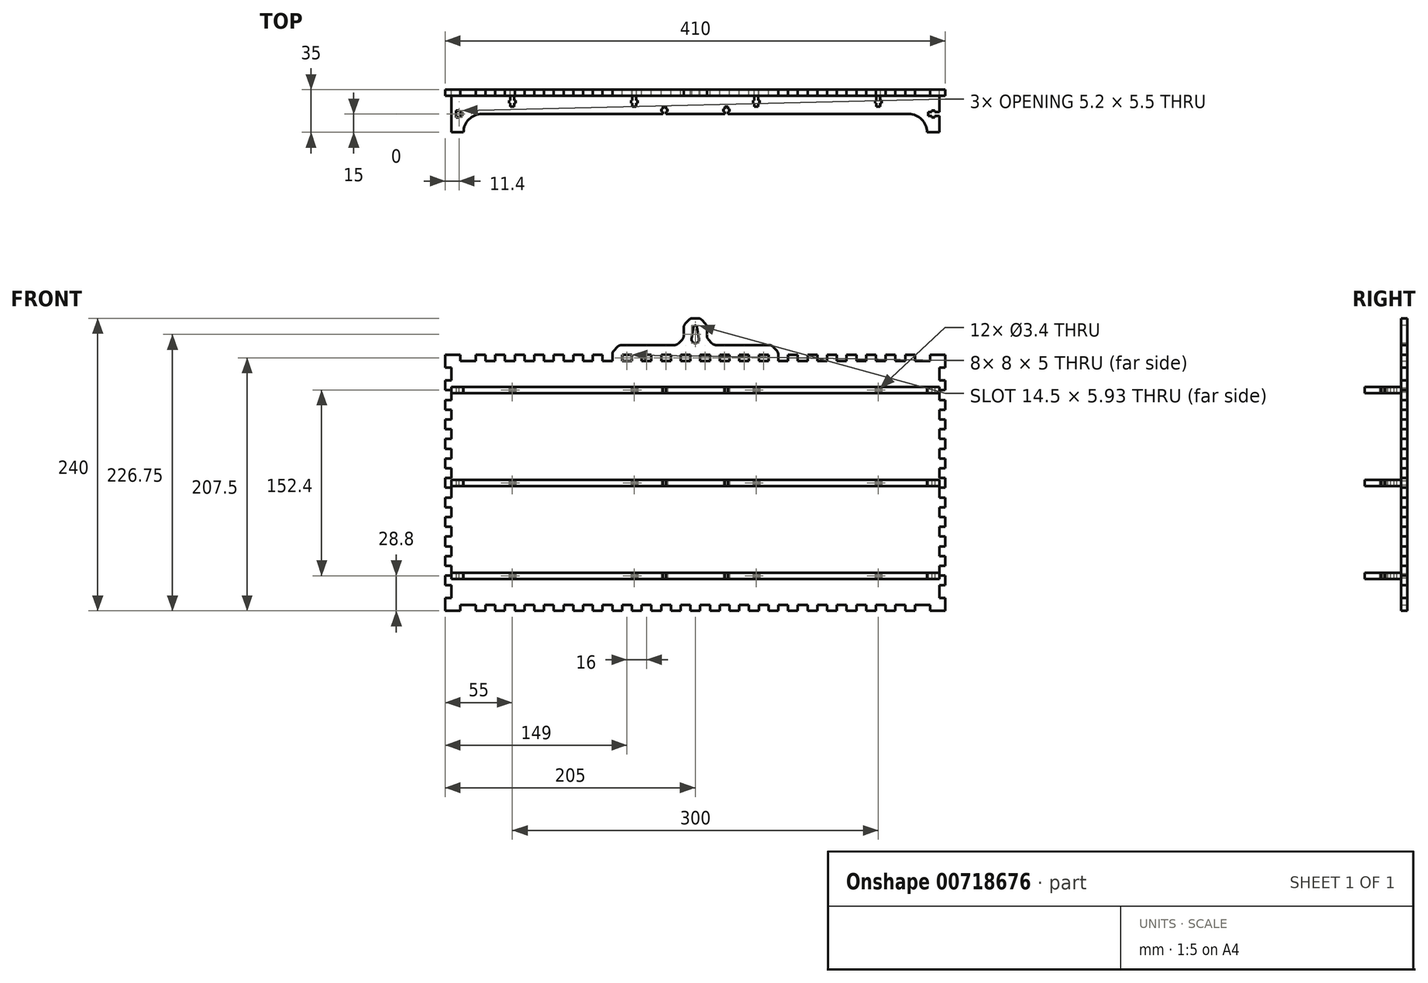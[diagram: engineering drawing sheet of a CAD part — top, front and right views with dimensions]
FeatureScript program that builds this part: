
annotation { "Feature Type Name" : "Feature", "Feature Type Description" : "" }
export const myFeature = defineFeature(function(context is Context, id is Id, definition is map)
    precondition{}
    {
        {
            var Q0;
            Q0=qCreatedBy(makeId("Front.planeOp"),FACE);
            var sketch = newSketch(context, id + "F0", { "sketchPlane" : qUnion([Q0])});
            skLineSegment(sketch, "E0", {"start": v(-100, 105) * mm, "end": v(-92, 105) * mm});
            skLineSegment(sketch, "E1", {"start": v(-92, 105) * mm, "end": v(-92, 100) * mm});
            skLineSegment(sketch, "E2", {"start": v(-92, 100) * mm, "end": v(-84, 100) * mm});
            skLineSegment(sketch, "E3", {"start": v(-84, 100) * mm, "end": v(-84, 105) * mm});
            skLineSegment(sketch, "E4", {"start": v(-84, 105) * mm, "end": v(-76, 105) * mm});
            skLineSegment(sketch, "E5", {"start": v(-76, 105) * mm, "end": v(-76, 100) * mm});
            skLineSegment(sketch, "E6", {"start": v(-76, 100) * mm, "end": v(-68, 100) * mm});
            skLineSegment(sketch, "E7", {"start": v(-68, 100) * mm, "end": v(-68, 105) * mm});
            skLineSegment(sketch, "E8", {"start": v(-68, 105) * mm, "end": v(-60, 105) * mm});
            skLineSegment(sketch, "E9", {"start": v(-60, 105) * mm, "end": v(-60, 100) * mm});
            skLineSegment(sketch, "E10", {"start": v(-60, 100) * mm, "end": v(-52, 100) * mm});
            skLineSegment(sketch, "E11", {"start": v(-52, 100) * mm, "end": v(-52, 105) * mm});
            skLineSegment(sketch, "E12", {"start": v(-52, 105) * mm, "end": v(-44, 105) * mm});
            skLineSegment(sketch, "E13", {"start": v(-44, 105) * mm, "end": v(-44, 100) * mm});
            skLineSegment(sketch, "E14", {"start": v(-44, 100) * mm, "end": v(-36, 100) * mm});
            skLineSegment(sketch, "E15", {"start": v(-36, 100) * mm, "end": v(-36, 105) * mm});
            skLineSegment(sketch, "E16", {"start": v(-36, 105) * mm, "end": v(-28, 105) * mm});
            skLineSegment(sketch, "E17", {"start": v(-28, 105) * mm, "end": v(-28, 100) * mm});
            skLineSegment(sketch, "E18", {"start": v(-28, 100) * mm, "end": v(-20, 100) * mm});
            skLineSegment(sketch, "E19", {"start": v(-20, 100) * mm, "end": v(-20, 105) * mm});
            skLineSegment(sketch, "E20", {"start": v(-20, 105) * mm, "end": v(-12, 105) * mm});
            skLineSegment(sketch, "E21", {"start": v(-12, 105) * mm, "end": v(-12, 100) * mm});
            skLineSegment(sketch, "E22", {"start": v(-12, 100) * mm, "end": v(-4, 100) * mm});
            skLineSegment(sketch, "E23", {"start": v(-4, 100) * mm, "end": v(-4, 105) * mm});
            skLineSegment(sketch, "E24", {"start": v(-4, 105) * mm, "end": v(4, 105) * mm});
            skLineSegment(sketch, "E25", {"start": v(4, 105) * mm, "end": v(4, 100) * mm});
            skLineSegment(sketch, "E26", {"start": v(4, 100) * mm, "end": v(12, 100) * mm});
            skLineSegment(sketch, "E27", {"start": v(12, 100) * mm, "end": v(12, 105) * mm});
            skLineSegment(sketch, "E28", {"start": v(12, 105) * mm, "end": v(20, 105) * mm});
            skLineSegment(sketch, "E29", {"start": v(20, 105) * mm, "end": v(20, 100) * mm});
            skLineSegment(sketch, "E30", {"start": v(20, 100) * mm, "end": v(28, 100) * mm});
            skLineSegment(sketch, "E31", {"start": v(28, 100) * mm, "end": v(28, 105) * mm});
            skLineSegment(sketch, "E32", {"start": v(28, 105) * mm, "end": v(36, 105) * mm});
            skLineSegment(sketch, "E33", {"start": v(36, 105) * mm, "end": v(36, 100) * mm});
            skLineSegment(sketch, "E34", {"start": v(36, 100) * mm, "end": v(44, 100) * mm});
            skLineSegment(sketch, "E35", {"start": v(44, 100) * mm, "end": v(44, 105) * mm});
            skLineSegment(sketch, "E36", {"start": v(44, 105) * mm, "end": v(52, 105) * mm});
            skLineSegment(sketch, "E37", {"start": v(52, 105) * mm, "end": v(52, 100) * mm});
            skLineSegment(sketch, "E38", {"start": v(52, 100) * mm, "end": v(60, 100) * mm});
            skLineSegment(sketch, "E39", {"start": v(60, 100) * mm, "end": v(60, 105) * mm});
            skLineSegment(sketch, "E40", {"start": v(60, 105) * mm, "end": v(68, 105) * mm});
            skLineSegment(sketch, "E41", {"start": v(68, 105) * mm, "end": v(68, 100) * mm});
            skLineSegment(sketch, "E42", {"start": v(68, 100) * mm, "end": v(76, 100) * mm});
            skLineSegment(sketch, "E43", {"start": v(76, 100) * mm, "end": v(76, 105) * mm});
            skLineSegment(sketch, "E44", {"start": v(76, 105) * mm, "end": v(84, 105) * mm});
            skLineSegment(sketch, "E45", {"start": v(84, 105) * mm, "end": v(84, 100) * mm});
            skLineSegment(sketch, "E46", {"start": v(84, 100) * mm, "end": v(92, 100) * mm});
            skLineSegment(sketch, "E47", {"start": v(92, 100) * mm, "end": v(92, 105) * mm});
            skLineSegment(sketch, "E48", {"start": v(92, 105) * mm, "end": v(100, 105) * mm});
            skLineSegment(sketch, "E49", {"start": v(100, 105) * mm, "end": v(100, 100) * mm});
            skLineSegment(sketch, "E50", {"start": v(100, 100) * mm, "end": v(108, 100) * mm});
            skLineSegment(sketch, "E51", {"start": v(108, 100) * mm, "end": v(108, 105) * mm});
            skLineSegment(sketch, "E52", {"start": v(108, 105) * mm, "end": v(116, 105) * mm});
            skLineSegment(sketch, "E53", {"start": v(116, 105) * mm, "end": v(116, 100) * mm});
            skLineSegment(sketch, "E54", {"start": v(116, 100) * mm, "end": v(124, 100) * mm});
            skLineSegment(sketch, "E55", {"start": v(124, 100) * mm, "end": v(124, 105) * mm});
            skLineSegment(sketch, "E56", {"start": v(124, 105) * mm, "end": v(132, 105) * mm});
            skLineSegment(sketch, "E57", {"start": v(132, 105) * mm, "end": v(132, 100) * mm});
            skLineSegment(sketch, "E58", {"start": v(132, 100) * mm, "end": v(140, 100) * mm});
            skLineSegment(sketch, "E59", {"start": v(140, 100) * mm, "end": v(140, 105) * mm});
            skLineSegment(sketch, "E60", {"start": v(140, 105) * mm, "end": v(148, 105) * mm});
            skLineSegment(sketch, "E61", {"start": v(148, 105) * mm, "end": v(148, 100) * mm});
            skLineSegment(sketch, "E62", {"start": v(148, 100) * mm, "end": v(156, 100) * mm});
            skLineSegment(sketch, "E63", {"start": v(156, 100) * mm, "end": v(156, 105) * mm});
            skLineSegment(sketch, "E64", {"start": v(156, 105) * mm, "end": v(164, 105) * mm});
            skLineSegment(sketch, "E65", {"start": v(164, 105) * mm, "end": v(164, 100) * mm});
            skLineSegment(sketch, "E66", {"start": v(164, 100) * mm, "end": v(172, 100) * mm});
            skLineSegment(sketch, "E67", {"start": v(172, 100) * mm, "end": v(172, 105) * mm});
            skLineSegment(sketch, "E68", {"start": v(172, 105) * mm, "end": v(180, 105) * mm});
            skLineSegment(sketch, "E69", {"start": v(180, 105) * mm, "end": v(180, 100) * mm});
            skLineSegment(sketch, "E70", {"start": v(180, 100) * mm, "end": v(192.5, 100) * mm});
            skLineSegment(sketch, "E71", {"start": v(192.5, 100) * mm, "end": v(192.5, 105) * mm});
            skLineSegment(sketch, "E72", {"start": v(192.5, 105) * mm, "end": v(205, 105) * mm});
            skLineSegment(sketch, "E73", {"start": v(205, 105) * mm, "end": v(205, 94.5) * mm});
            skLineSegment(sketch, "E74", {"start": v(205, 94.5) * mm, "end": v(200, 94.5) * mm});
            skLineSegment(sketch, "E75", {"start": v(200, 94.5) * mm, "end": v(200, 84) * mm});
            skLineSegment(sketch, "E76", {"start": v(200, 84) * mm, "end": v(205, 84) * mm});
            skLineSegment(sketch, "E77", {"start": v(205, 84) * mm, "end": v(205, 76) * mm});
            skLineSegment(sketch, "E78", {"start": v(205, 76) * mm, "end": v(200, 76) * mm});
            skLineSegment(sketch, "E79", {"start": v(200, 76) * mm, "end": v(200, 68) * mm});
            skLineSegment(sketch, "E80", {"start": v(200, 68) * mm, "end": v(205, 68) * mm});
            skLineSegment(sketch, "E81", {"start": v(205, 68) * mm, "end": v(205, 60) * mm});
            skLineSegment(sketch, "E82", {"start": v(205, 60) * mm, "end": v(200, 60) * mm});
            skLineSegment(sketch, "E83", {"start": v(200, 60) * mm, "end": v(200, 52) * mm});
            skLineSegment(sketch, "E84", {"start": v(200, 52) * mm, "end": v(205, 52) * mm});
            skLineSegment(sketch, "E85", {"start": v(205, 52) * mm, "end": v(205, 44) * mm});
            skLineSegment(sketch, "E86", {"start": v(205, 44) * mm, "end": v(200, 44) * mm});
            skLineSegment(sketch, "E87", {"start": v(200, 44) * mm, "end": v(200, 36) * mm});
            skLineSegment(sketch, "E88", {"start": v(200, 36) * mm, "end": v(205, 36) * mm});
            skLineSegment(sketch, "E89", {"start": v(205, 36) * mm, "end": v(205, 28) * mm});
            skLineSegment(sketch, "E90", {"start": v(205, 28) * mm, "end": v(200, 28) * mm});
            skLineSegment(sketch, "E91", {"start": v(200, 28) * mm, "end": v(200, 20) * mm});
            skLineSegment(sketch, "E92", {"start": v(200, 20) * mm, "end": v(205, 20) * mm});
            skLineSegment(sketch, "E93", {"start": v(205, 20) * mm, "end": v(205, 12) * mm});
            skLineSegment(sketch, "E94", {"start": v(205, 12) * mm, "end": v(200, 12) * mm});
            skLineSegment(sketch, "E95", {"start": v(200, 12) * mm, "end": v(200, 4) * mm});
            skLineSegment(sketch, "E96", {"start": v(200, 4) * mm, "end": v(205, 4) * mm});
            skLineSegment(sketch, "E97", {"start": v(205, 4) * mm, "end": v(205, -4) * mm});
            skLineSegment(sketch, "E98", {"start": v(205, -4) * mm, "end": v(200, -4) * mm});
            skLineSegment(sketch, "E99", {"start": v(200, -4) * mm, "end": v(200, -12) * mm});
            skLineSegment(sketch, "E100", {"start": v(200, -12) * mm, "end": v(205, -12) * mm});
            skLineSegment(sketch, "E101", {"start": v(205, -12) * mm, "end": v(205, -20) * mm});
            skLineSegment(sketch, "E102", {"start": v(205, -20) * mm, "end": v(200, -20) * mm});
            skLineSegment(sketch, "E103", {"start": v(200, -20) * mm, "end": v(200, -28) * mm});
            skLineSegment(sketch, "E104", {"start": v(200, -28) * mm, "end": v(205, -28) * mm});
            skLineSegment(sketch, "E105", {"start": v(205, -28) * mm, "end": v(205, -36) * mm});
            skLineSegment(sketch, "E106", {"start": v(205, -36) * mm, "end": v(200, -36) * mm});
            skLineSegment(sketch, "E107", {"start": v(200, -36) * mm, "end": v(200, -44) * mm});
            skLineSegment(sketch, "E108", {"start": v(200, -44) * mm, "end": v(205, -44) * mm});
            skLineSegment(sketch, "E109", {"start": v(205, -44) * mm, "end": v(205, -52) * mm});
            skLineSegment(sketch, "E110", {"start": v(205, -52) * mm, "end": v(200, -52) * mm});
            skLineSegment(sketch, "E111", {"start": v(200, -52) * mm, "end": v(200, -60) * mm});
            skLineSegment(sketch, "E112", {"start": v(200, -60) * mm, "end": v(205, -60) * mm});
            skLineSegment(sketch, "E113", {"start": v(205, -60) * mm, "end": v(205, -68) * mm});
            skLineSegment(sketch, "E114", {"start": v(205, -68) * mm, "end": v(200, -68) * mm});
            skLineSegment(sketch, "E115", {"start": v(200, -68) * mm, "end": v(200, -76) * mm});
            skLineSegment(sketch, "E116", {"start": v(200, -76) * mm, "end": v(205, -76) * mm});
            skLineSegment(sketch, "E117", {"start": v(205, -76) * mm, "end": v(205, -84) * mm});
            skLineSegment(sketch, "E118", {"start": v(205, -84) * mm, "end": v(200, -84) * mm});
            skLineSegment(sketch, "E119", {"start": v(200, -84) * mm, "end": v(200, -94.5) * mm});
            skLineSegment(sketch, "E120", {"start": v(200, -94.5) * mm, "end": v(205, -94.5) * mm});
            skLineSegment(sketch, "E121", {"start": v(205, -94.5) * mm, "end": v(205, -105) * mm});
            skLineSegment(sketch, "E122", {"start": v(205, -105) * mm, "end": v(192.5, -105) * mm});
            skLineSegment(sketch, "E123", {"start": v(192.5, -105) * mm, "end": v(192.5, -100) * mm});
            skLineSegment(sketch, "E124", {"start": v(192.5, -100) * mm, "end": v(180, -100) * mm});
            skLineSegment(sketch, "E125", {"start": v(180, -100) * mm, "end": v(180, -105) * mm});
            skLineSegment(sketch, "E126", {"start": v(180, -105) * mm, "end": v(172, -105) * mm});
            skLineSegment(sketch, "E127", {"start": v(172, -105) * mm, "end": v(172, -100) * mm});
            skLineSegment(sketch, "E128", {"start": v(172, -100) * mm, "end": v(164, -100) * mm});
            skLineSegment(sketch, "E129", {"start": v(164, -100) * mm, "end": v(164, -105) * mm});
            skLineSegment(sketch, "E130", {"start": v(164, -105) * mm, "end": v(156, -105) * mm});
            skLineSegment(sketch, "E131", {"start": v(156, -105) * mm, "end": v(156, -100) * mm});
            skLineSegment(sketch, "E132", {"start": v(156, -100) * mm, "end": v(148, -100) * mm});
            skLineSegment(sketch, "E133", {"start": v(148, -100) * mm, "end": v(148, -105) * mm});
            skLineSegment(sketch, "E134", {"start": v(148, -105) * mm, "end": v(140, -105) * mm});
            skLineSegment(sketch, "E135", {"start": v(140, -105) * mm, "end": v(140, -100) * mm});
            skLineSegment(sketch, "E136", {"start": v(140, -100) * mm, "end": v(132, -100) * mm});
            skLineSegment(sketch, "E137", {"start": v(132, -100) * mm, "end": v(132, -105) * mm});
            skLineSegment(sketch, "E138", {"start": v(132, -105) * mm, "end": v(124, -105) * mm});
            skLineSegment(sketch, "E139", {"start": v(124, -105) * mm, "end": v(124, -100) * mm});
            skLineSegment(sketch, "E140", {"start": v(124, -100) * mm, "end": v(116, -100) * mm});
            skLineSegment(sketch, "E141", {"start": v(116, -100) * mm, "end": v(116, -105) * mm});
            skLineSegment(sketch, "E142", {"start": v(116, -105) * mm, "end": v(108, -105) * mm});
            skLineSegment(sketch, "E143", {"start": v(108, -105) * mm, "end": v(108, -100) * mm});
            skLineSegment(sketch, "E144", {"start": v(108, -100) * mm, "end": v(100, -100) * mm});
            skLineSegment(sketch, "E145", {"start": v(100, -100) * mm, "end": v(100, -105) * mm});
            skLineSegment(sketch, "E146", {"start": v(100, -105) * mm, "end": v(92, -105) * mm});
            skLineSegment(sketch, "E147", {"start": v(92, -105) * mm, "end": v(92, -100) * mm});
            skLineSegment(sketch, "E148", {"start": v(92, -100) * mm, "end": v(84, -100) * mm});
            skLineSegment(sketch, "E149", {"start": v(84, -100) * mm, "end": v(84, -105) * mm});
            skLineSegment(sketch, "E150", {"start": v(84, -105) * mm, "end": v(76, -105) * mm});
            skLineSegment(sketch, "E151", {"start": v(76, -105) * mm, "end": v(76, -100) * mm});
            skLineSegment(sketch, "E152", {"start": v(76, -100) * mm, "end": v(68, -100) * mm});
            skLineSegment(sketch, "E153", {"start": v(68, -100) * mm, "end": v(68, -105) * mm});
            skLineSegment(sketch, "E154", {"start": v(68, -105) * mm, "end": v(60, -105) * mm});
            skLineSegment(sketch, "E155", {"start": v(60, -105) * mm, "end": v(60, -100) * mm});
            skLineSegment(sketch, "E156", {"start": v(60, -100) * mm, "end": v(52, -100) * mm});
            skLineSegment(sketch, "E157", {"start": v(52, -100) * mm, "end": v(52, -105) * mm});
            skLineSegment(sketch, "E158", {"start": v(52, -105) * mm, "end": v(44, -105) * mm});
            skLineSegment(sketch, "E159", {"start": v(44, -105) * mm, "end": v(44, -100) * mm});
            skLineSegment(sketch, "E160", {"start": v(44, -100) * mm, "end": v(36, -100) * mm});
            skLineSegment(sketch, "E161", {"start": v(36, -100) * mm, "end": v(36, -105) * mm});
            skLineSegment(sketch, "E162", {"start": v(36, -105) * mm, "end": v(28, -105) * mm});
            skLineSegment(sketch, "E163", {"start": v(28, -105) * mm, "end": v(28, -100) * mm});
            skLineSegment(sketch, "E164", {"start": v(28, -100) * mm, "end": v(20, -100) * mm});
            skLineSegment(sketch, "E165", {"start": v(20, -100) * mm, "end": v(20, -105) * mm});
            skLineSegment(sketch, "E166", {"start": v(20, -105) * mm, "end": v(12, -105) * mm});
            skLineSegment(sketch, "E167", {"start": v(12, -105) * mm, "end": v(12, -100) * mm});
            skLineSegment(sketch, "E168", {"start": v(12, -100) * mm, "end": v(4, -100) * mm});
            skLineSegment(sketch, "E169", {"start": v(4, -100) * mm, "end": v(4, -105) * mm});
            skLineSegment(sketch, "E170", {"start": v(4, -105) * mm, "end": v(-4, -105) * mm});
            skLineSegment(sketch, "E171", {"start": v(-4, -105) * mm, "end": v(-4, -100) * mm});
            skLineSegment(sketch, "E172", {"start": v(-4, -100) * mm, "end": v(-12, -100) * mm});
            skLineSegment(sketch, "E173", {"start": v(-12, -100) * mm, "end": v(-12, -105) * mm});
            skLineSegment(sketch, "E174", {"start": v(-12, -105) * mm, "end": v(-20, -105) * mm});
            skLineSegment(sketch, "E175", {"start": v(-20, -105) * mm, "end": v(-20, -100) * mm});
            skLineSegment(sketch, "E176", {"start": v(-20, -100) * mm, "end": v(-28, -100) * mm});
            skLineSegment(sketch, "E177", {"start": v(-28, -100) * mm, "end": v(-28, -105) * mm});
            skLineSegment(sketch, "E178", {"start": v(-28, -105) * mm, "end": v(-36, -105) * mm});
            skLineSegment(sketch, "E179", {"start": v(-36, -105) * mm, "end": v(-36, -100) * mm});
            skLineSegment(sketch, "E180", {"start": v(-36, -100) * mm, "end": v(-44, -100) * mm});
            skLineSegment(sketch, "E181", {"start": v(-44, -100) * mm, "end": v(-44, -105) * mm});
            skLineSegment(sketch, "E182", {"start": v(-44, -105) * mm, "end": v(-52, -105) * mm});
            skLineSegment(sketch, "E183", {"start": v(-52, -105) * mm, "end": v(-52, -100) * mm});
            skLineSegment(sketch, "E184", {"start": v(-52, -100) * mm, "end": v(-60, -100) * mm});
            skLineSegment(sketch, "E185", {"start": v(-60, -100) * mm, "end": v(-60, -105) * mm});
            skLineSegment(sketch, "E186", {"start": v(-60, -105) * mm, "end": v(-68, -105) * mm});
            skLineSegment(sketch, "E187", {"start": v(-68, -105) * mm, "end": v(-68, -100) * mm});
            skLineSegment(sketch, "E188", {"start": v(-68, -100) * mm, "end": v(-76, -100) * mm});
            skLineSegment(sketch, "E189", {"start": v(-76, -100) * mm, "end": v(-76, -105) * mm});
            skLineSegment(sketch, "E190", {"start": v(-76, -105) * mm, "end": v(-84, -105) * mm});
            skLineSegment(sketch, "E191", {"start": v(-84, -105) * mm, "end": v(-84, -100) * mm});
            skLineSegment(sketch, "E192", {"start": v(-84, -100) * mm, "end": v(-92, -100) * mm});
            skLineSegment(sketch, "E193", {"start": v(-92, -100) * mm, "end": v(-92, -105) * mm});
            skLineSegment(sketch, "E194", {"start": v(-92, -105) * mm, "end": v(-100, -105) * mm});
            skLineSegment(sketch, "E195", {"start": v(-100, -105) * mm, "end": v(-100, -100) * mm});
            skLineSegment(sketch, "E196", {"start": v(-100, -100) * mm, "end": v(-108, -100) * mm});
            skLineSegment(sketch, "E197", {"start": v(-108, -100) * mm, "end": v(-108, -105) * mm});
            skLineSegment(sketch, "E198", {"start": v(-108, -105) * mm, "end": v(-116, -105) * mm});
            skLineSegment(sketch, "E199", {"start": v(-116, -105) * mm, "end": v(-116, -100) * mm});
            skLineSegment(sketch, "E200", {"start": v(-116, -100) * mm, "end": v(-124, -100) * mm});
            skLineSegment(sketch, "E201", {"start": v(-124, -100) * mm, "end": v(-124, -105) * mm});
            skLineSegment(sketch, "E202", {"start": v(-124, -105) * mm, "end": v(-132, -105) * mm});
            skLineSegment(sketch, "E203", {"start": v(-132, -105) * mm, "end": v(-132, -100) * mm});
            skLineSegment(sketch, "E204", {"start": v(-132, -100) * mm, "end": v(-140, -100) * mm});
            skLineSegment(sketch, "E205", {"start": v(-140, -100) * mm, "end": v(-140, -105) * mm});
            skLineSegment(sketch, "E206", {"start": v(-140, -105) * mm, "end": v(-148, -105) * mm});
            skLineSegment(sketch, "E207", {"start": v(-148, -105) * mm, "end": v(-148, -100) * mm});
            skLineSegment(sketch, "E208", {"start": v(-148, -100) * mm, "end": v(-156, -100) * mm});
            skLineSegment(sketch, "E209", {"start": v(-156, -100) * mm, "end": v(-156, -105) * mm});
            skLineSegment(sketch, "E210", {"start": v(-156, -105) * mm, "end": v(-164, -105) * mm});
            skLineSegment(sketch, "E211", {"start": v(-164, -105) * mm, "end": v(-164, -100) * mm});
            skLineSegment(sketch, "E212", {"start": v(-164, -100) * mm, "end": v(-172, -100) * mm});
            skLineSegment(sketch, "E213", {"start": v(-172, -100) * mm, "end": v(-172, -105) * mm});
            skLineSegment(sketch, "E214", {"start": v(-172, -105) * mm, "end": v(-180, -105) * mm});
            skLineSegment(sketch, "E215", {"start": v(-180, -105) * mm, "end": v(-180, -100) * mm});
            skLineSegment(sketch, "E216", {"start": v(-180, -100) * mm, "end": v(-192.5, -100) * mm});
            skLineSegment(sketch, "E217", {"start": v(-192.5, -100) * mm, "end": v(-192.5, -105) * mm});
            skLineSegment(sketch, "E218", {"start": v(-192.5, -105) * mm, "end": v(-205, -105) * mm});
            skLineSegment(sketch, "E219", {"start": v(-205, -105) * mm, "end": v(-205, -94.5) * mm});
            skLineSegment(sketch, "E220", {"start": v(-205, -94.5) * mm, "end": v(-200, -94.5) * mm});
            skLineSegment(sketch, "E221", {"start": v(-200, -94.5) * mm, "end": v(-200, -84) * mm});
            skLineSegment(sketch, "E222", {"start": v(-200, -84) * mm, "end": v(-205, -84) * mm});
            skLineSegment(sketch, "E223", {"start": v(-205, -84) * mm, "end": v(-205, -76) * mm});
            skLineSegment(sketch, "E224", {"start": v(-205, -76) * mm, "end": v(-200, -76) * mm});
            skLineSegment(sketch, "E225", {"start": v(-200, -76) * mm, "end": v(-200, -68) * mm});
            skLineSegment(sketch, "E226", {"start": v(-200, -68) * mm, "end": v(-205, -68) * mm});
            skLineSegment(sketch, "E227", {"start": v(-205, -68) * mm, "end": v(-205, -60) * mm});
            skLineSegment(sketch, "E228", {"start": v(-205, -60) * mm, "end": v(-200, -60) * mm});
            skLineSegment(sketch, "E229", {"start": v(-200, -60) * mm, "end": v(-200, -52) * mm});
            skLineSegment(sketch, "E230", {"start": v(-200, -52) * mm, "end": v(-205, -52) * mm});
            skLineSegment(sketch, "E231", {"start": v(-205, -52) * mm, "end": v(-205, -44) * mm});
            skLineSegment(sketch, "E232", {"start": v(-205, -44) * mm, "end": v(-200, -44) * mm});
            skLineSegment(sketch, "E233", {"start": v(-200, -44) * mm, "end": v(-200, -36) * mm});
            skLineSegment(sketch, "E234", {"start": v(-200, -36) * mm, "end": v(-205, -36) * mm});
            skLineSegment(sketch, "E235", {"start": v(-205, -36) * mm, "end": v(-205, -28) * mm});
            skLineSegment(sketch, "E236", {"start": v(-205, -28) * mm, "end": v(-200, -28) * mm});
            skLineSegment(sketch, "E237", {"start": v(-200, -28) * mm, "end": v(-200, -20) * mm});
            skLineSegment(sketch, "E238", {"start": v(-200, -20) * mm, "end": v(-205, -20) * mm});
            skLineSegment(sketch, "E239", {"start": v(-205, -20) * mm, "end": v(-205, -12) * mm});
            skLineSegment(sketch, "E240", {"start": v(-205, -12) * mm, "end": v(-200, -12) * mm});
            skLineSegment(sketch, "E241", {"start": v(-200, -12) * mm, "end": v(-200, -4) * mm});
            skLineSegment(sketch, "E242", {"start": v(-200, -4) * mm, "end": v(-205, -4) * mm});
            skLineSegment(sketch, "E243", {"start": v(-205, -4) * mm, "end": v(-205, 4) * mm});
            skLineSegment(sketch, "E244", {"start": v(-205, 4) * mm, "end": v(-200, 4) * mm});
            skLineSegment(sketch, "E245", {"start": v(-200, 4) * mm, "end": v(-200, 12) * mm});
            skLineSegment(sketch, "E246", {"start": v(-200, 12) * mm, "end": v(-205, 12) * mm});
            skLineSegment(sketch, "E247", {"start": v(-205, 12) * mm, "end": v(-205, 20) * mm});
            skLineSegment(sketch, "E248", {"start": v(-205, 20) * mm, "end": v(-200, 20) * mm});
            skLineSegment(sketch, "E249", {"start": v(-200, 20) * mm, "end": v(-200, 28) * mm});
            skLineSegment(sketch, "E250", {"start": v(-200, 28) * mm, "end": v(-205, 28) * mm});
            skLineSegment(sketch, "E251", {"start": v(-205, 28) * mm, "end": v(-205, 36) * mm});
            skLineSegment(sketch, "E252", {"start": v(-205, 36) * mm, "end": v(-200, 36) * mm});
            skLineSegment(sketch, "E253", {"start": v(-200, 36) * mm, "end": v(-200, 44) * mm});
            skLineSegment(sketch, "E254", {"start": v(-200, 44) * mm, "end": v(-205, 44) * mm});
            skLineSegment(sketch, "E255", {"start": v(-205, 44) * mm, "end": v(-205, 52) * mm});
            skLineSegment(sketch, "E256", {"start": v(-205, 52) * mm, "end": v(-200, 52) * mm});
            skLineSegment(sketch, "E257", {"start": v(-200, 52) * mm, "end": v(-200, 60) * mm});
            skLineSegment(sketch, "E258", {"start": v(-200, 60) * mm, "end": v(-205, 60) * mm});
            skLineSegment(sketch, "E259", {"start": v(-205, 60) * mm, "end": v(-205, 68) * mm});
            skLineSegment(sketch, "E260", {"start": v(-205, 68) * mm, "end": v(-200, 68) * mm});
            skLineSegment(sketch, "E261", {"start": v(-200, 68) * mm, "end": v(-200, 76) * mm});
            skLineSegment(sketch, "E262", {"start": v(-200, 76) * mm, "end": v(-205, 76) * mm});
            skLineSegment(sketch, "E263", {"start": v(-205, 76) * mm, "end": v(-205, 84) * mm});
            skLineSegment(sketch, "E264", {"start": v(-205, 84) * mm, "end": v(-200, 84) * mm});
            skLineSegment(sketch, "E265", {"start": v(-200, 84) * mm, "end": v(-200, 94.5) * mm});
            skLineSegment(sketch, "E266", {"start": v(-200, 94.5) * mm, "end": v(-205, 94.5) * mm});
            skLineSegment(sketch, "E267", {"start": v(-205, 94.5) * mm, "end": v(-205, 105) * mm});
            skLineSegment(sketch, "E268", {"start": v(-205, 105) * mm, "end": v(-192.5, 105) * mm});
            skLineSegment(sketch, "E269", {"start": v(-192.5, 105) * mm, "end": v(-192.5, 100) * mm});
            skLineSegment(sketch, "E270", {"start": v(-192.5, 100) * mm, "end": v(-180, 100) * mm});
            skLineSegment(sketch, "E271", {"start": v(-180, 100) * mm, "end": v(-180, 105) * mm});
            skLineSegment(sketch, "E272", {"start": v(-180, 105) * mm, "end": v(-172, 105) * mm});
            skLineSegment(sketch, "E273", {"start": v(-172, 105) * mm, "end": v(-172, 100) * mm});
            skLineSegment(sketch, "E274", {"start": v(-172, 100) * mm, "end": v(-164, 100) * mm});
            skLineSegment(sketch, "E275", {"start": v(-164, 100) * mm, "end": v(-164, 105) * mm});
            skLineSegment(sketch, "E276", {"start": v(-164, 105) * mm, "end": v(-156, 105) * mm});
            skLineSegment(sketch, "E277", {"start": v(-156, 105) * mm, "end": v(-156, 100) * mm});
            skLineSegment(sketch, "E278", {"start": v(-156, 100) * mm, "end": v(-148, 100) * mm});
            skLineSegment(sketch, "E279", {"start": v(-148, 100) * mm, "end": v(-148, 105) * mm});
            skLineSegment(sketch, "E280", {"start": v(-148, 105) * mm, "end": v(-140, 105) * mm});
            skLineSegment(sketch, "E281", {"start": v(-140, 105) * mm, "end": v(-140, 100) * mm});
            skLineSegment(sketch, "E282", {"start": v(-140, 100) * mm, "end": v(-132, 100) * mm});
            skLineSegment(sketch, "E283", {"start": v(-132, 100) * mm, "end": v(-132, 105) * mm});
            skLineSegment(sketch, "E284", {"start": v(-132, 105) * mm, "end": v(-124, 105) * mm});
            skLineSegment(sketch, "E285", {"start": v(-124, 105) * mm, "end": v(-124, 100) * mm});
            skLineSegment(sketch, "E286", {"start": v(-124, 100) * mm, "end": v(-116, 100) * mm});
            skLineSegment(sketch, "E287", {"start": v(-116, 100) * mm, "end": v(-116, 105) * mm});
            skLineSegment(sketch, "E288", {"start": v(-116, 105) * mm, "end": v(-108, 105) * mm});
            skLineSegment(sketch, "E289", {"start": v(-108, 105) * mm, "end": v(-108, 100) * mm});
            skLineSegment(sketch, "E290", {"start": v(-108, 100) * mm, "end": v(-100, 100) * mm});
            skLineSegment(sketch, "E291", {"start": v(-100, 100) * mm, "end": v(-100, 105) * mm});
            skSolve(sketch);
        }
        {
            var Q0;
            Q0=makeQuery(id+"F0.imprint","IMPRINT",FACE,{"disambiguationData":[TD([[makeQuery(id+"F0.imprint","IMPRINT",EDGE,{"derivedFrom":sQuery(id+"F0.wireOp",EDGE,"E0")}),-1.0]])]});
            extrude(context, id + "F1", {"entities" : qUnion([Q0]), "depth" : 5 * mm, "offsetDistance" : 25 * mm});
        }
        {
            var Q0;
            Q0=makeQuery(id+"F1.opExtrude","CAP_FACE",FACE,{"disambiguationData":[OSD([sQuery(id+"F0.wireOp",EDGE,"E0"),sQuery(id+"F0.wireOp",EDGE,"E1"),sQuery(id+"F0.wireOp",EDGE,"E2"),sQuery(id+"F0.wireOp",EDGE,"E3"),sQuery(id+"F0.wireOp",EDGE,"E4"),sQuery(id+"F0.wireOp",EDGE,"E5"),sQuery(id+"F0.wireOp",EDGE,"E6"),sQuery(id+"F0.wireOp",EDGE,"E7"),sQuery(id+"F0.wireOp",EDGE,"E8"),sQuery(id+"F0.wireOp",EDGE,"E9"),sQuery(id+"F0.wireOp",EDGE,"E10"),sQuery(id+"F0.wireOp",EDGE,"E11"),sQuery(id+"F0.wireOp",EDGE,"E12"),sQuery(id+"F0.wireOp",EDGE,"E13"),sQuery(id+"F0.wireOp",EDGE,"E14"),sQuery(id+"F0.wireOp",EDGE,"E15"),sQuery(id+"F0.wireOp",EDGE,"E16"),sQuery(id+"F0.wireOp",EDGE,"E17"),sQuery(id+"F0.wireOp",EDGE,"E18"),sQuery(id+"F0.wireOp",EDGE,"E19"),sQuery(id+"F0.wireOp",EDGE,"E20"),sQuery(id+"F0.wireOp",EDGE,"E21"),sQuery(id+"F0.wireOp",EDGE,"E22"),sQuery(id+"F0.wireOp",EDGE,"E23"),sQuery(id+"F0.wireOp",EDGE,"E24"),sQuery(id+"F0.wireOp",EDGE,"E25"),sQuery(id+"F0.wireOp",EDGE,"E26"),sQuery(id+"F0.wireOp",EDGE,"E27"),sQuery(id+"F0.wireOp",EDGE,"E28"),sQuery(id+"F0.wireOp",EDGE,"E29"),sQuery(id+"F0.wireOp",EDGE,"E30"),sQuery(id+"F0.wireOp",EDGE,"E31"),sQuery(id+"F0.wireOp",EDGE,"E32"),sQuery(id+"F0.wireOp",EDGE,"E33"),sQuery(id+"F0.wireOp",EDGE,"E34"),sQuery(id+"F0.wireOp",EDGE,"E35"),sQuery(id+"F0.wireOp",EDGE,"E36"),sQuery(id+"F0.wireOp",EDGE,"E37"),sQuery(id+"F0.wireOp",EDGE,"E38"),sQuery(id+"F0.wireOp",EDGE,"E39"),sQuery(id+"F0.wireOp",EDGE,"E40"),sQuery(id+"F0.wireOp",EDGE,"E41"),sQuery(id+"F0.wireOp",EDGE,"E42"),sQuery(id+"F0.wireOp",EDGE,"E43"),sQuery(id+"F0.wireOp",EDGE,"E44"),sQuery(id+"F0.wireOp",EDGE,"E45"),sQuery(id+"F0.wireOp",EDGE,"E46"),sQuery(id+"F0.wireOp",EDGE,"E47"),sQuery(id+"F0.wireOp",EDGE,"E48"),sQuery(id+"F0.wireOp",EDGE,"E49"),sQuery(id+"F0.wireOp",EDGE,"E50"),sQuery(id+"F0.wireOp",EDGE,"E51"),sQuery(id+"F0.wireOp",EDGE,"E52"),sQuery(id+"F0.wireOp",EDGE,"E53"),sQuery(id+"F0.wireOp",EDGE,"E54"),sQuery(id+"F0.wireOp",EDGE,"E55"),sQuery(id+"F0.wireOp",EDGE,"E56"),sQuery(id+"F0.wireOp",EDGE,"E57"),sQuery(id+"F0.wireOp",EDGE,"E58"),sQuery(id+"F0.wireOp",EDGE,"E59"),sQuery(id+"F0.wireOp",EDGE,"E60"),sQuery(id+"F0.wireOp",EDGE,"E61"),sQuery(id+"F0.wireOp",EDGE,"E62"),sQuery(id+"F0.wireOp",EDGE,"E63"),sQuery(id+"F0.wireOp",EDGE,"E64"),sQuery(id+"F0.wireOp",EDGE,"E65"),sQuery(id+"F0.wireOp",EDGE,"E66"),sQuery(id+"F0.wireOp",EDGE,"E67"),sQuery(id+"F0.wireOp",EDGE,"E68"),sQuery(id+"F0.wireOp",EDGE,"E69"),sQuery(id+"F0.wireOp",EDGE,"E70"),sQuery(id+"F0.wireOp",EDGE,"E71"),sQuery(id+"F0.wireOp",EDGE,"E72"),sQuery(id+"F0.wireOp",EDGE,"E73"),sQuery(id+"F0.wireOp",EDGE,"E74"),sQuery(id+"F0.wireOp",EDGE,"E75"),sQuery(id+"F0.wireOp",EDGE,"E76"),sQuery(id+"F0.wireOp",EDGE,"E77"),sQuery(id+"F0.wireOp",EDGE,"E78"),sQuery(id+"F0.wireOp",EDGE,"E79"),sQuery(id+"F0.wireOp",EDGE,"E80"),sQuery(id+"F0.wireOp",EDGE,"E81"),sQuery(id+"F0.wireOp",EDGE,"E82"),sQuery(id+"F0.wireOp",EDGE,"E83"),sQuery(id+"F0.wireOp",EDGE,"E84"),sQuery(id+"F0.wireOp",EDGE,"E85"),sQuery(id+"F0.wireOp",EDGE,"E86"),sQuery(id+"F0.wireOp",EDGE,"E87"),sQuery(id+"F0.wireOp",EDGE,"E88"),sQuery(id+"F0.wireOp",EDGE,"E89"),sQuery(id+"F0.wireOp",EDGE,"E90"),sQuery(id+"F0.wireOp",EDGE,"E91"),sQuery(id+"F0.wireOp",EDGE,"E92"),sQuery(id+"F0.wireOp",EDGE,"E93"),sQuery(id+"F0.wireOp",EDGE,"E94"),sQuery(id+"F0.wireOp",EDGE,"E95"),sQuery(id+"F0.wireOp",EDGE,"E96"),sQuery(id+"F0.wireOp",EDGE,"E97"),sQuery(id+"F0.wireOp",EDGE,"E98"),sQuery(id+"F0.wireOp",EDGE,"E99"),sQuery(id+"F0.wireOp",EDGE,"E100"),sQuery(id+"F0.wireOp",EDGE,"E101"),sQuery(id+"F0.wireOp",EDGE,"E102"),sQuery(id+"F0.wireOp",EDGE,"E103"),sQuery(id+"F0.wireOp",EDGE,"E104"),sQuery(id+"F0.wireOp",EDGE,"E105"),sQuery(id+"F0.wireOp",EDGE,"E106"),sQuery(id+"F0.wireOp",EDGE,"E107"),sQuery(id+"F0.wireOp",EDGE,"E108"),sQuery(id+"F0.wireOp",EDGE,"E109"),sQuery(id+"F0.wireOp",EDGE,"E110"),sQuery(id+"F0.wireOp",EDGE,"E111"),sQuery(id+"F0.wireOp",EDGE,"E112"),sQuery(id+"F0.wireOp",EDGE,"E113"),sQuery(id+"F0.wireOp",EDGE,"E114"),sQuery(id+"F0.wireOp",EDGE,"E115"),sQuery(id+"F0.wireOp",EDGE,"E116"),sQuery(id+"F0.wireOp",EDGE,"E117"),sQuery(id+"F0.wireOp",EDGE,"E118"),sQuery(id+"F0.wireOp",EDGE,"E119"),sQuery(id+"F0.wireOp",EDGE,"E120"),sQuery(id+"F0.wireOp",EDGE,"E121"),sQuery(id+"F0.wireOp",EDGE,"E122"),sQuery(id+"F0.wireOp",EDGE,"E123"),sQuery(id+"F0.wireOp",EDGE,"E124"),sQuery(id+"F0.wireOp",EDGE,"E125"),sQuery(id+"F0.wireOp",EDGE,"E126"),sQuery(id+"F0.wireOp",EDGE,"E127"),sQuery(id+"F0.wireOp",EDGE,"E128"),sQuery(id+"F0.wireOp",EDGE,"E129"),sQuery(id+"F0.wireOp",EDGE,"E130"),sQuery(id+"F0.wireOp",EDGE,"E131"),sQuery(id+"F0.wireOp",EDGE,"E132"),sQuery(id+"F0.wireOp",EDGE,"E133"),sQuery(id+"F0.wireOp",EDGE,"E134"),sQuery(id+"F0.wireOp",EDGE,"E135"),sQuery(id+"F0.wireOp",EDGE,"E136"),sQuery(id+"F0.wireOp",EDGE,"E137"),sQuery(id+"F0.wireOp",EDGE,"E138"),sQuery(id+"F0.wireOp",EDGE,"E139"),sQuery(id+"F0.wireOp",EDGE,"E140"),sQuery(id+"F0.wireOp",EDGE,"E141"),sQuery(id+"F0.wireOp",EDGE,"E142"),sQuery(id+"F0.wireOp",EDGE,"E143"),sQuery(id+"F0.wireOp",EDGE,"E144"),sQuery(id+"F0.wireOp",EDGE,"E145"),sQuery(id+"F0.wireOp",EDGE,"E146"),sQuery(id+"F0.wireOp",EDGE,"E147"),sQuery(id+"F0.wireOp",EDGE,"E148"),sQuery(id+"F0.wireOp",EDGE,"E149"),sQuery(id+"F0.wireOp",EDGE,"E150"),sQuery(id+"F0.wireOp",EDGE,"E151"),sQuery(id+"F0.wireOp",EDGE,"E152"),sQuery(id+"F0.wireOp",EDGE,"E153"),sQuery(id+"F0.wireOp",EDGE,"E154"),sQuery(id+"F0.wireOp",EDGE,"E155"),sQuery(id+"F0.wireOp",EDGE,"E156"),sQuery(id+"F0.wireOp",EDGE,"E157"),sQuery(id+"F0.wireOp",EDGE,"E158"),sQuery(id+"F0.wireOp",EDGE,"E159"),sQuery(id+"F0.wireOp",EDGE,"E160"),sQuery(id+"F0.wireOp",EDGE,"E161"),sQuery(id+"F0.wireOp",EDGE,"E162"),sQuery(id+"F0.wireOp",EDGE,"E163"),sQuery(id+"F0.wireOp",EDGE,"E164"),sQuery(id+"F0.wireOp",EDGE,"E165"),sQuery(id+"F0.wireOp",EDGE,"E166"),sQuery(id+"F0.wireOp",EDGE,"E167"),sQuery(id+"F0.wireOp",EDGE,"E168"),sQuery(id+"F0.wireOp",EDGE,"E169"),sQuery(id+"F0.wireOp",EDGE,"E170"),sQuery(id+"F0.wireOp",EDGE,"E171"),sQuery(id+"F0.wireOp",EDGE,"E172"),sQuery(id+"F0.wireOp",EDGE,"E173"),sQuery(id+"F0.wireOp",EDGE,"E174"),sQuery(id+"F0.wireOp",EDGE,"E175"),sQuery(id+"F0.wireOp",EDGE,"E176"),sQuery(id+"F0.wireOp",EDGE,"E177"),sQuery(id+"F0.wireOp",EDGE,"E178"),sQuery(id+"F0.wireOp",EDGE,"E179"),sQuery(id+"F0.wireOp",EDGE,"E180"),sQuery(id+"F0.wireOp",EDGE,"E181"),sQuery(id+"F0.wireOp",EDGE,"E182"),sQuery(id+"F0.wireOp",EDGE,"E183"),sQuery(id+"F0.wireOp",EDGE,"E184"),sQuery(id+"F0.wireOp",EDGE,"E185"),sQuery(id+"F0.wireOp",EDGE,"E186"),sQuery(id+"F0.wireOp",EDGE,"E187"),sQuery(id+"F0.wireOp",EDGE,"E188"),sQuery(id+"F0.wireOp",EDGE,"E189"),sQuery(id+"F0.wireOp",EDGE,"E190"),sQuery(id+"F0.wireOp",EDGE,"E191"),sQuery(id+"F0.wireOp",EDGE,"E192"),sQuery(id+"F0.wireOp",EDGE,"E193"),sQuery(id+"F0.wireOp",EDGE,"E194"),sQuery(id+"F0.wireOp",EDGE,"E195"),sQuery(id+"F0.wireOp",EDGE,"E196"),sQuery(id+"F0.wireOp",EDGE,"E197"),sQuery(id+"F0.wireOp",EDGE,"E198"),sQuery(id+"F0.wireOp",EDGE,"E199"),sQuery(id+"F0.wireOp",EDGE,"E200"),sQuery(id+"F0.wireOp",EDGE,"E201"),sQuery(id+"F0.wireOp",EDGE,"E202"),sQuery(id+"F0.wireOp",EDGE,"E203"),sQuery(id+"F0.wireOp",EDGE,"E204"),sQuery(id+"F0.wireOp",EDGE,"E205"),sQuery(id+"F0.wireOp",EDGE,"E206"),sQuery(id+"F0.wireOp",EDGE,"E207"),sQuery(id+"F0.wireOp",EDGE,"E208"),sQuery(id+"F0.wireOp",EDGE,"E209"),sQuery(id+"F0.wireOp",EDGE,"E210"),sQuery(id+"F0.wireOp",EDGE,"E211"),sQuery(id+"F0.wireOp",EDGE,"E212"),sQuery(id+"F0.wireOp",EDGE,"E213"),sQuery(id+"F0.wireOp",EDGE,"E214"),sQuery(id+"F0.wireOp",EDGE,"E215"),sQuery(id+"F0.wireOp",EDGE,"E216"),sQuery(id+"F0.wireOp",EDGE,"E217"),sQuery(id+"F0.wireOp",EDGE,"E218"),sQuery(id+"F0.wireOp",EDGE,"E219"),sQuery(id+"F0.wireOp",EDGE,"E220"),sQuery(id+"F0.wireOp",EDGE,"E221"),sQuery(id+"F0.wireOp",EDGE,"E222"),sQuery(id+"F0.wireOp",EDGE,"E223"),sQuery(id+"F0.wireOp",EDGE,"E224"),sQuery(id+"F0.wireOp",EDGE,"E225"),sQuery(id+"F0.wireOp",EDGE,"E226"),sQuery(id+"F0.wireOp",EDGE,"E227"),sQuery(id+"F0.wireOp",EDGE,"E228"),sQuery(id+"F0.wireOp",EDGE,"E229"),sQuery(id+"F0.wireOp",EDGE,"E230"),sQuery(id+"F0.wireOp",EDGE,"E231"),sQuery(id+"F0.wireOp",EDGE,"E232"),sQuery(id+"F0.wireOp",EDGE,"E233"),sQuery(id+"F0.wireOp",EDGE,"E234"),sQuery(id+"F0.wireOp",EDGE,"E235"),sQuery(id+"F0.wireOp",EDGE,"E236"),sQuery(id+"F0.wireOp",EDGE,"E237"),sQuery(id+"F0.wireOp",EDGE,"E238"),sQuery(id+"F0.wireOp",EDGE,"E239"),sQuery(id+"F0.wireOp",EDGE,"E240"),sQuery(id+"F0.wireOp",EDGE,"E241"),sQuery(id+"F0.wireOp",EDGE,"E242"),sQuery(id+"F0.wireOp",EDGE,"E243"),sQuery(id+"F0.wireOp",EDGE,"E244"),sQuery(id+"F0.wireOp",EDGE,"E245"),sQuery(id+"F0.wireOp",EDGE,"E246"),sQuery(id+"F0.wireOp",EDGE,"E247"),sQuery(id+"F0.wireOp",EDGE,"E248"),sQuery(id+"F0.wireOp",EDGE,"E249"),sQuery(id+"F0.wireOp",EDGE,"E250"),sQuery(id+"F0.wireOp",EDGE,"E251"),sQuery(id+"F0.wireOp",EDGE,"E252"),sQuery(id+"F0.wireOp",EDGE,"E253"),sQuery(id+"F0.wireOp",EDGE,"E254"),sQuery(id+"F0.wireOp",EDGE,"E255"),sQuery(id+"F0.wireOp",EDGE,"E256"),sQuery(id+"F0.wireOp",EDGE,"E257"),sQuery(id+"F0.wireOp",EDGE,"E258"),sQuery(id+"F0.wireOp",EDGE,"E259"),sQuery(id+"F0.wireOp",EDGE,"E260"),sQuery(id+"F0.wireOp",EDGE,"E261"),sQuery(id+"F0.wireOp",EDGE,"E262"),sQuery(id+"F0.wireOp",EDGE,"E263"),sQuery(id+"F0.wireOp",EDGE,"E264"),sQuery(id+"F0.wireOp",EDGE,"E265"),sQuery(id+"F0.wireOp",EDGE,"E266"),sQuery(id+"F0.wireOp",EDGE,"E267"),sQuery(id+"F0.wireOp",EDGE,"E268"),sQuery(id+"F0.wireOp",EDGE,"E269"),sQuery(id+"F0.wireOp",EDGE,"E270"),sQuery(id+"F0.wireOp",EDGE,"E271"),sQuery(id+"F0.wireOp",EDGE,"E272"),sQuery(id+"F0.wireOp",EDGE,"E273"),sQuery(id+"F0.wireOp",EDGE,"E274"),sQuery(id+"F0.wireOp",EDGE,"E275"),sQuery(id+"F0.wireOp",EDGE,"E276"),sQuery(id+"F0.wireOp",EDGE,"E277"),sQuery(id+"F0.wireOp",EDGE,"E278"),sQuery(id+"F0.wireOp",EDGE,"E279"),sQuery(id+"F0.wireOp",EDGE,"E280"),sQuery(id+"F0.wireOp",EDGE,"E281"),sQuery(id+"F0.wireOp",EDGE,"E282"),sQuery(id+"F0.wireOp",EDGE,"E283"),sQuery(id+"F0.wireOp",EDGE,"E284"),sQuery(id+"F0.wireOp",EDGE,"E285"),sQuery(id+"F0.wireOp",EDGE,"E286"),sQuery(id+"F0.wireOp",EDGE,"E287"),sQuery(id+"F0.wireOp",EDGE,"E288"),sQuery(id+"F0.wireOp",EDGE,"E289"),sQuery(id+"F0.wireOp",EDGE,"E290"),sQuery(id+"F0.wireOp",EDGE,"E291")])],"isStart":false});
            var sketch = newSketch(context, id + "F2", { "sketchPlane" : qUnion([Q0])});
            skLineSegment(sketch, "E292", {"start": v(0, 0) * mm, "end": v(0, 105) * mm, "construction": true});
            skLineSegment(sketch, "E293", {"start": v(0, 105) * mm, "end": v(0, 135) * mm, "construction": true});
            skLineSegment(sketch, "E294", {"start": v(0, 135) * mm, "end": v(-1.84, 135) * mm});
            skLineSegment(sketch, "E295", {"start": v(-5.48, 133.43) * mm, "end": v(-8.13, 130.63) * mm});
            skLineSegment(sketch, "E296", {"start": v(-9.5, 127.2) * mm, "end": v(-9.5, 120.8) * mm});
            skLineSegment(sketch, "E297", {"start": v(-10.85, 117.37) * mm, "end": v(-13.5, 114.57) * mm});
            skLineSegment(sketch, "E298", {"start": v(-17.14, 113) * mm, "end": v(-60.35, 113) * mm});
            skLineSegment(sketch, "E299", {"start": v(-63.99, 111.43) * mm, "end": v(-66.64, 108.63) * mm});
            skLineSegment(sketch, "E300", {"start": v(-68, 105.2) * mm, "end": v(-68, 105) * mm});
            skPoint(sketch, "E301.visualSharp", {"position": v(-4, 135) * mm});
            skArc(sketch, "E301.filletArc", {"start": v(-1.84, 135) * mm, "mid": v(-3.82, 134.6) * mm, "end": v(-5.48, 133.43) * mm});
            skPoint(sketch, "E302.visualSharp", {"position": v(-9.5, 129.18) * mm});
            skArc(sketch, "E302.filletArc", {"start": v(-8.13, 130.63) * mm, "mid": v(-9.14, 129.04) * mm, "end": v(-9.5, 127.2) * mm});
            skPoint(sketch, "E303.visualSharp", {"position": v(-9.5, 118.82) * mm});
            skArc(sketch, "E303.filletArc", {"start": v(-10.85, 117.37) * mm, "mid": v(-9.84, 118.96) * mm, "end": v(-9.5, 120.8) * mm});
            skPoint(sketch, "E304.visualSharp", {"position": v(-14.98, 113) * mm});
            skArc(sketch, "E304.filletArc", {"start": v(-17.14, 113) * mm, "mid": v(-15.16, 113.4) * mm, "end": v(-13.5, 114.57) * mm});
            skPoint(sketch, "E305.visualSharp", {"position": v(-62.5, 113) * mm});
            skArc(sketch, "E305.filletArc", {"start": v(-60.35, 113) * mm, "mid": v(-62.33, 112.6) * mm, "end": v(-63.99, 111.43) * mm});
            skPoint(sketch, "E306.visualSharp", {"position": v(-68, 107.18) * mm});
            skArc(sketch, "E306.filletArc", {"start": v(-66.64, 108.63) * mm, "mid": v(-67.65, 107.04) * mm, "end": v(-68, 105.2) * mm});
            skLineSegment(sketch, "E307", {"start": v(-68, 105) * mm, "end": v(0, 105) * mm});
            skLineSegment(sketch, "E308.MirrorCS", {"start": v(0, 135) * mm, "end": v(1.84, 135) * mm});
            skLineSegment(sketch, "E309.MirrorCS", {"start": v(68, 105.2) * mm, "end": v(68, 105) * mm});
            skArc(sketch, "E310.MirrorCS", {"start": v(17.14, 113) * mm, "mid": v(15.16, 113.4) * mm, "end": v(13.5, 114.57) * mm});
            skArc(sketch, "E311.MirrorCS", {"start": v(1.84, 135) * mm, "mid": v(3.82, 134.6) * mm, "end": v(5.48, 133.43) * mm});
            skArc(sketch, "E312.MirrorCS", {"start": v(60.35, 113) * mm, "mid": v(62.33, 112.6) * mm, "end": v(63.99, 111.43) * mm});
            skArc(sketch, "E313.MirrorCS", {"start": v(8.13, 130.63) * mm, "mid": v(9.14, 129.04) * mm, "end": v(9.5, 127.2) * mm});
            skArc(sketch, "E314.MirrorCS", {"start": v(10.85, 117.37) * mm, "mid": v(9.84, 118.96) * mm, "end": v(9.5, 120.8) * mm});
            skArc(sketch, "E315.MirrorCS", {"start": v(66.64, 108.63) * mm, "mid": v(67.65, 107.04) * mm, "end": v(68, 105.2) * mm});
            skLineSegment(sketch, "E316.MirrorCS", {"start": v(63.99, 111.43) * mm, "end": v(66.64, 108.63) * mm});
            skPoint(sketch, "E317.MirrorP", {"position": v(4, 135) * mm});
            skPoint(sketch, "E318.MirrorP", {"position": v(14.98, 113) * mm});
            skPoint(sketch, "E319.MirrorP", {"position": v(9.5, 118.82) * mm});
            skLineSegment(sketch, "E320.MirrorCS", {"start": v(10.85, 117.37) * mm, "end": v(13.5, 114.57) * mm});
            skLineSegment(sketch, "E321.MirrorCS", {"start": v(17.14, 113) * mm, "end": v(60.35, 113) * mm});
            skLineSegment(sketch, "E322.MirrorCS", {"start": v(5.48, 133.43) * mm, "end": v(8.13, 130.63) * mm});
            skLineSegment(sketch, "E323.MirrorCS", {"start": v(68, 105) * mm, "end": v(0, 105) * mm});
            skPoint(sketch, "E324.MirrorP", {"position": v(9.5, 129.18) * mm});
            skPoint(sketch, "E325.MirrorP", {"position": v(62.5, 113) * mm});
            skPoint(sketch, "E326.MirrorP", {"position": v(68, 107.18) * mm});
            skLineSegment(sketch, "E327.MirrorCS", {"start": v(9.5, 127.2) * mm, "end": v(9.5, 120.8) * mm});
            skCircle(sketch, "E328", {"center": v(0, 127.5) * mm, "radius": 1.5 * mm});
            skCircle(sketch, "E329", {"center": v(0, 117.5) * mm, "radius": 3 * mm});
            skLineSegment(sketch, "E330", {"start": v(-1.48, 127.73) * mm, "end": v(-2.97, 117.95) * mm});
            skLineSegment(sketch, "E331", {"start": v(1.48, 127.73) * mm, "end": v(2.97, 117.95) * mm});
            skSolve(sketch);
        }
        {
            var Q0;
            Q0=makeQuery(id+"F2.imprint","IMPRINT",FACE,{"disambiguationData":[TD([[makeQuery(id+"F2.imprint","IMPRINT",EDGE,{"derivedFrom":sQuery(id+"F2.wireOp",EDGE,"E294")}),1.0]])]});
            extrude(context, id + "F3", {"entities" : qUnion([Q0]), "operationType" : NewBodyOperationType.ADD, "oppositeDirection" : true, "depth" : 5 * mm, "offsetDistance" : 25 * mm});
        }
        {
            var Q0;
            Q0=makeQuery(id+"F3.boolean.opBoolean","MERGE",FACE,{"derivedFrom":[makeQuery(id+"F1.opExtrude","CAP_FACE",FACE,{"disambiguationData":[OSD([sQuery(id+"F0.wireOp",EDGE,"E0"),sQuery(id+"F0.wireOp",EDGE,"E1"),sQuery(id+"F0.wireOp",EDGE,"E2"),sQuery(id+"F0.wireOp",EDGE,"E3"),sQuery(id+"F0.wireOp",EDGE,"E4"),sQuery(id+"F0.wireOp",EDGE,"E5"),sQuery(id+"F0.wireOp",EDGE,"E6"),sQuery(id+"F0.wireOp",EDGE,"E7"),sQuery(id+"F0.wireOp",EDGE,"E8"),sQuery(id+"F0.wireOp",EDGE,"E9"),sQuery(id+"F0.wireOp",EDGE,"E10"),sQuery(id+"F0.wireOp",EDGE,"E11"),sQuery(id+"F0.wireOp",EDGE,"E12"),sQuery(id+"F0.wireOp",EDGE,"E13"),sQuery(id+"F0.wireOp",EDGE,"E14"),sQuery(id+"F0.wireOp",EDGE,"E15"),sQuery(id+"F0.wireOp",EDGE,"E16"),sQuery(id+"F0.wireOp",EDGE,"E17"),sQuery(id+"F0.wireOp",EDGE,"E18"),sQuery(id+"F0.wireOp",EDGE,"E19"),sQuery(id+"F0.wireOp",EDGE,"E20"),sQuery(id+"F0.wireOp",EDGE,"E21"),sQuery(id+"F0.wireOp",EDGE,"E22"),sQuery(id+"F0.wireOp",EDGE,"E23"),sQuery(id+"F0.wireOp",EDGE,"E24"),sQuery(id+"F0.wireOp",EDGE,"E25"),sQuery(id+"F0.wireOp",EDGE,"E26"),sQuery(id+"F0.wireOp",EDGE,"E27"),sQuery(id+"F0.wireOp",EDGE,"E28"),sQuery(id+"F0.wireOp",EDGE,"E29"),sQuery(id+"F0.wireOp",EDGE,"E30"),sQuery(id+"F0.wireOp",EDGE,"E31"),sQuery(id+"F0.wireOp",EDGE,"E32"),sQuery(id+"F0.wireOp",EDGE,"E33"),sQuery(id+"F0.wireOp",EDGE,"E34"),sQuery(id+"F0.wireOp",EDGE,"E35"),sQuery(id+"F0.wireOp",EDGE,"E36"),sQuery(id+"F0.wireOp",EDGE,"E37"),sQuery(id+"F0.wireOp",EDGE,"E38"),sQuery(id+"F0.wireOp",EDGE,"E39"),sQuery(id+"F0.wireOp",EDGE,"E40"),sQuery(id+"F0.wireOp",EDGE,"E41"),sQuery(id+"F0.wireOp",EDGE,"E42"),sQuery(id+"F0.wireOp",EDGE,"E43"),sQuery(id+"F0.wireOp",EDGE,"E44"),sQuery(id+"F0.wireOp",EDGE,"E45"),sQuery(id+"F0.wireOp",EDGE,"E46"),sQuery(id+"F0.wireOp",EDGE,"E47"),sQuery(id+"F0.wireOp",EDGE,"E48"),sQuery(id+"F0.wireOp",EDGE,"E49"),sQuery(id+"F0.wireOp",EDGE,"E50"),sQuery(id+"F0.wireOp",EDGE,"E51"),sQuery(id+"F0.wireOp",EDGE,"E52"),sQuery(id+"F0.wireOp",EDGE,"E53"),sQuery(id+"F0.wireOp",EDGE,"E54"),sQuery(id+"F0.wireOp",EDGE,"E55"),sQuery(id+"F0.wireOp",EDGE,"E56"),sQuery(id+"F0.wireOp",EDGE,"E57"),sQuery(id+"F0.wireOp",EDGE,"E58"),sQuery(id+"F0.wireOp",EDGE,"E59"),sQuery(id+"F0.wireOp",EDGE,"E60"),sQuery(id+"F0.wireOp",EDGE,"E61"),sQuery(id+"F0.wireOp",EDGE,"E62"),sQuery(id+"F0.wireOp",EDGE,"E63"),sQuery(id+"F0.wireOp",EDGE,"E64"),sQuery(id+"F0.wireOp",EDGE,"E65"),sQuery(id+"F0.wireOp",EDGE,"E66"),sQuery(id+"F0.wireOp",EDGE,"E67"),sQuery(id+"F0.wireOp",EDGE,"E68"),sQuery(id+"F0.wireOp",EDGE,"E69"),sQuery(id+"F0.wireOp",EDGE,"E70"),sQuery(id+"F0.wireOp",EDGE,"E71"),sQuery(id+"F0.wireOp",EDGE,"E72"),sQuery(id+"F0.wireOp",EDGE,"E73"),sQuery(id+"F0.wireOp",EDGE,"E74"),sQuery(id+"F0.wireOp",EDGE,"E75"),sQuery(id+"F0.wireOp",EDGE,"E76"),sQuery(id+"F0.wireOp",EDGE,"E77"),sQuery(id+"F0.wireOp",EDGE,"E78"),sQuery(id+"F0.wireOp",EDGE,"E79"),sQuery(id+"F0.wireOp",EDGE,"E80"),sQuery(id+"F0.wireOp",EDGE,"E81"),sQuery(id+"F0.wireOp",EDGE,"E82"),sQuery(id+"F0.wireOp",EDGE,"E83"),sQuery(id+"F0.wireOp",EDGE,"E84"),sQuery(id+"F0.wireOp",EDGE,"E85"),sQuery(id+"F0.wireOp",EDGE,"E86"),sQuery(id+"F0.wireOp",EDGE,"E87"),sQuery(id+"F0.wireOp",EDGE,"E88"),sQuery(id+"F0.wireOp",EDGE,"E89"),sQuery(id+"F0.wireOp",EDGE,"E90"),sQuery(id+"F0.wireOp",EDGE,"E91"),sQuery(id+"F0.wireOp",EDGE,"E92"),sQuery(id+"F0.wireOp",EDGE,"E93"),sQuery(id+"F0.wireOp",EDGE,"E94"),sQuery(id+"F0.wireOp",EDGE,"E95"),sQuery(id+"F0.wireOp",EDGE,"E96"),sQuery(id+"F0.wireOp",EDGE,"E97"),sQuery(id+"F0.wireOp",EDGE,"E98"),sQuery(id+"F0.wireOp",EDGE,"E99"),sQuery(id+"F0.wireOp",EDGE,"E100"),sQuery(id+"F0.wireOp",EDGE,"E101"),sQuery(id+"F0.wireOp",EDGE,"E102"),sQuery(id+"F0.wireOp",EDGE,"E103"),sQuery(id+"F0.wireOp",EDGE,"E104"),sQuery(id+"F0.wireOp",EDGE,"E105"),sQuery(id+"F0.wireOp",EDGE,"E106"),sQuery(id+"F0.wireOp",EDGE,"E107"),sQuery(id+"F0.wireOp",EDGE,"E108"),sQuery(id+"F0.wireOp",EDGE,"E109"),sQuery(id+"F0.wireOp",EDGE,"E110"),sQuery(id+"F0.wireOp",EDGE,"E111"),sQuery(id+"F0.wireOp",EDGE,"E112"),sQuery(id+"F0.wireOp",EDGE,"E113"),sQuery(id+"F0.wireOp",EDGE,"E114"),sQuery(id+"F0.wireOp",EDGE,"E115"),sQuery(id+"F0.wireOp",EDGE,"E116"),sQuery(id+"F0.wireOp",EDGE,"E117"),sQuery(id+"F0.wireOp",EDGE,"E118"),sQuery(id+"F0.wireOp",EDGE,"E119"),sQuery(id+"F0.wireOp",EDGE,"E120"),sQuery(id+"F0.wireOp",EDGE,"E121"),sQuery(id+"F0.wireOp",EDGE,"E122"),sQuery(id+"F0.wireOp",EDGE,"E123"),sQuery(id+"F0.wireOp",EDGE,"E124"),sQuery(id+"F0.wireOp",EDGE,"E125"),sQuery(id+"F0.wireOp",EDGE,"E126"),sQuery(id+"F0.wireOp",EDGE,"E127"),sQuery(id+"F0.wireOp",EDGE,"E128"),sQuery(id+"F0.wireOp",EDGE,"E129"),sQuery(id+"F0.wireOp",EDGE,"E130"),sQuery(id+"F0.wireOp",EDGE,"E131"),sQuery(id+"F0.wireOp",EDGE,"E132"),sQuery(id+"F0.wireOp",EDGE,"E133"),sQuery(id+"F0.wireOp",EDGE,"E134"),sQuery(id+"F0.wireOp",EDGE,"E135"),sQuery(id+"F0.wireOp",EDGE,"E136"),sQuery(id+"F0.wireOp",EDGE,"E137"),sQuery(id+"F0.wireOp",EDGE,"E138"),sQuery(id+"F0.wireOp",EDGE,"E139"),sQuery(id+"F0.wireOp",EDGE,"E140"),sQuery(id+"F0.wireOp",EDGE,"E141"),sQuery(id+"F0.wireOp",EDGE,"E142"),sQuery(id+"F0.wireOp",EDGE,"E143"),sQuery(id+"F0.wireOp",EDGE,"E144"),sQuery(id+"F0.wireOp",EDGE,"E145"),sQuery(id+"F0.wireOp",EDGE,"E146"),sQuery(id+"F0.wireOp",EDGE,"E147"),sQuery(id+"F0.wireOp",EDGE,"E148"),sQuery(id+"F0.wireOp",EDGE,"E149"),sQuery(id+"F0.wireOp",EDGE,"E150"),sQuery(id+"F0.wireOp",EDGE,"E151"),sQuery(id+"F0.wireOp",EDGE,"E152"),sQuery(id+"F0.wireOp",EDGE,"E153"),sQuery(id+"F0.wireOp",EDGE,"E154"),sQuery(id+"F0.wireOp",EDGE,"E155"),sQuery(id+"F0.wireOp",EDGE,"E156"),sQuery(id+"F0.wireOp",EDGE,"E157"),sQuery(id+"F0.wireOp",EDGE,"E158"),sQuery(id+"F0.wireOp",EDGE,"E159"),sQuery(id+"F0.wireOp",EDGE,"E160"),sQuery(id+"F0.wireOp",EDGE,"E161"),sQuery(id+"F0.wireOp",EDGE,"E162"),sQuery(id+"F0.wireOp",EDGE,"E163"),sQuery(id+"F0.wireOp",EDGE,"E164"),sQuery(id+"F0.wireOp",EDGE,"E165"),sQuery(id+"F0.wireOp",EDGE,"E166"),sQuery(id+"F0.wireOp",EDGE,"E167"),sQuery(id+"F0.wireOp",EDGE,"E168"),sQuery(id+"F0.wireOp",EDGE,"E169"),sQuery(id+"F0.wireOp",EDGE,"E170"),sQuery(id+"F0.wireOp",EDGE,"E171"),sQuery(id+"F0.wireOp",EDGE,"E172"),sQuery(id+"F0.wireOp",EDGE,"E173"),sQuery(id+"F0.wireOp",EDGE,"E174"),sQuery(id+"F0.wireOp",EDGE,"E175"),sQuery(id+"F0.wireOp",EDGE,"E176"),sQuery(id+"F0.wireOp",EDGE,"E177"),sQuery(id+"F0.wireOp",EDGE,"E178"),sQuery(id+"F0.wireOp",EDGE,"E179"),sQuery(id+"F0.wireOp",EDGE,"E180"),sQuery(id+"F0.wireOp",EDGE,"E181"),sQuery(id+"F0.wireOp",EDGE,"E182"),sQuery(id+"F0.wireOp",EDGE,"E183"),sQuery(id+"F0.wireOp",EDGE,"E184"),sQuery(id+"F0.wireOp",EDGE,"E185"),sQuery(id+"F0.wireOp",EDGE,"E186"),sQuery(id+"F0.wireOp",EDGE,"E187"),sQuery(id+"F0.wireOp",EDGE,"E188"),sQuery(id+"F0.wireOp",EDGE,"E189"),sQuery(id+"F0.wireOp",EDGE,"E190"),sQuery(id+"F0.wireOp",EDGE,"E191"),sQuery(id+"F0.wireOp",EDGE,"E192"),sQuery(id+"F0.wireOp",EDGE,"E193"),sQuery(id+"F0.wireOp",EDGE,"E194"),sQuery(id+"F0.wireOp",EDGE,"E195"),sQuery(id+"F0.wireOp",EDGE,"E196"),sQuery(id+"F0.wireOp",EDGE,"E197"),sQuery(id+"F0.wireOp",EDGE,"E198"),sQuery(id+"F0.wireOp",EDGE,"E199"),sQuery(id+"F0.wireOp",EDGE,"E200"),sQuery(id+"F0.wireOp",EDGE,"E201"),sQuery(id+"F0.wireOp",EDGE,"E202"),sQuery(id+"F0.wireOp",EDGE,"E203"),sQuery(id+"F0.wireOp",EDGE,"E204"),sQuery(id+"F0.wireOp",EDGE,"E205"),sQuery(id+"F0.wireOp",EDGE,"E206"),sQuery(id+"F0.wireOp",EDGE,"E207"),sQuery(id+"F0.wireOp",EDGE,"E208"),sQuery(id+"F0.wireOp",EDGE,"E209"),sQuery(id+"F0.wireOp",EDGE,"E210"),sQuery(id+"F0.wireOp",EDGE,"E211"),sQuery(id+"F0.wireOp",EDGE,"E212"),sQuery(id+"F0.wireOp",EDGE,"E213"),sQuery(id+"F0.wireOp",EDGE,"E214"),sQuery(id+"F0.wireOp",EDGE,"E215"),sQuery(id+"F0.wireOp",EDGE,"E216"),sQuery(id+"F0.wireOp",EDGE,"E217"),sQuery(id+"F0.wireOp",EDGE,"E218"),sQuery(id+"F0.wireOp",EDGE,"E219"),sQuery(id+"F0.wireOp",EDGE,"E220"),sQuery(id+"F0.wireOp",EDGE,"E221"),sQuery(id+"F0.wireOp",EDGE,"E222"),sQuery(id+"F0.wireOp",EDGE,"E223"),sQuery(id+"F0.wireOp",EDGE,"E224"),sQuery(id+"F0.wireOp",EDGE,"E225"),sQuery(id+"F0.wireOp",EDGE,"E226"),sQuery(id+"F0.wireOp",EDGE,"E227"),sQuery(id+"F0.wireOp",EDGE,"E228"),sQuery(id+"F0.wireOp",EDGE,"E229"),sQuery(id+"F0.wireOp",EDGE,"E230"),sQuery(id+"F0.wireOp",EDGE,"E231"),sQuery(id+"F0.wireOp",EDGE,"E232"),sQuery(id+"F0.wireOp",EDGE,"E233"),sQuery(id+"F0.wireOp",EDGE,"E234"),sQuery(id+"F0.wireOp",EDGE,"E235"),sQuery(id+"F0.wireOp",EDGE,"E236"),sQuery(id+"F0.wireOp",EDGE,"E237"),sQuery(id+"F0.wireOp",EDGE,"E238"),sQuery(id+"F0.wireOp",EDGE,"E239"),sQuery(id+"F0.wireOp",EDGE,"E240"),sQuery(id+"F0.wireOp",EDGE,"E241"),sQuery(id+"F0.wireOp",EDGE,"E242"),sQuery(id+"F0.wireOp",EDGE,"E243"),sQuery(id+"F0.wireOp",EDGE,"E244"),sQuery(id+"F0.wireOp",EDGE,"E245"),sQuery(id+"F0.wireOp",EDGE,"E246"),sQuery(id+"F0.wireOp",EDGE,"E247"),sQuery(id+"F0.wireOp",EDGE,"E248"),sQuery(id+"F0.wireOp",EDGE,"E249"),sQuery(id+"F0.wireOp",EDGE,"E250"),sQuery(id+"F0.wireOp",EDGE,"E251"),sQuery(id+"F0.wireOp",EDGE,"E252"),sQuery(id+"F0.wireOp",EDGE,"E253"),sQuery(id+"F0.wireOp",EDGE,"E254"),sQuery(id+"F0.wireOp",EDGE,"E255"),sQuery(id+"F0.wireOp",EDGE,"E256"),sQuery(id+"F0.wireOp",EDGE,"E257"),sQuery(id+"F0.wireOp",EDGE,"E258"),sQuery(id+"F0.wireOp",EDGE,"E259"),sQuery(id+"F0.wireOp",EDGE,"E260"),sQuery(id+"F0.wireOp",EDGE,"E261"),sQuery(id+"F0.wireOp",EDGE,"E262"),sQuery(id+"F0.wireOp",EDGE,"E263"),sQuery(id+"F0.wireOp",EDGE,"E264"),sQuery(id+"F0.wireOp",EDGE,"E265"),sQuery(id+"F0.wireOp",EDGE,"E266"),sQuery(id+"F0.wireOp",EDGE,"E267"),sQuery(id+"F0.wireOp",EDGE,"E268"),sQuery(id+"F0.wireOp",EDGE,"E269"),sQuery(id+"F0.wireOp",EDGE,"E270"),sQuery(id+"F0.wireOp",EDGE,"E271"),sQuery(id+"F0.wireOp",EDGE,"E272"),sQuery(id+"F0.wireOp",EDGE,"E273"),sQuery(id+"F0.wireOp",EDGE,"E274"),sQuery(id+"F0.wireOp",EDGE,"E275"),sQuery(id+"F0.wireOp",EDGE,"E276"),sQuery(id+"F0.wireOp",EDGE,"E277"),sQuery(id+"F0.wireOp",EDGE,"E278"),sQuery(id+"F0.wireOp",EDGE,"E279"),sQuery(id+"F0.wireOp",EDGE,"E280"),sQuery(id+"F0.wireOp",EDGE,"E281"),sQuery(id+"F0.wireOp",EDGE,"E282"),sQuery(id+"F0.wireOp",EDGE,"E283"),sQuery(id+"F0.wireOp",EDGE,"E284"),sQuery(id+"F0.wireOp",EDGE,"E285"),sQuery(id+"F0.wireOp",EDGE,"E286"),sQuery(id+"F0.wireOp",EDGE,"E287"),sQuery(id+"F0.wireOp",EDGE,"E288"),sQuery(id+"F0.wireOp",EDGE,"E289"),sQuery(id+"F0.wireOp",EDGE,"E290"),sQuery(id+"F0.wireOp",EDGE,"E291")])],"isStart":false}),makeQuery(id+"F3.opExtrude","CAP_FACE",FACE,{"disambiguationData":[OSD([sQuery(id+"F2.wireOp",EDGE,"E294"),sQuery(id+"F2.wireOp",EDGE,"E295"),sQuery(id+"F2.wireOp",EDGE,"E296"),sQuery(id+"F2.wireOp",EDGE,"E297"),sQuery(id+"F2.wireOp",EDGE,"E298"),sQuery(id+"F2.wireOp",EDGE,"E299"),sQuery(id+"F2.wireOp",EDGE,"E300"),sQuery(id+"F2.wireOp",EDGE,"E301.filletArc"),sQuery(id+"F2.wireOp",EDGE,"E302.filletArc"),sQuery(id+"F2.wireOp",EDGE,"E303.filletArc"),sQuery(id+"F2.wireOp",EDGE,"E304.filletArc"),sQuery(id+"F2.wireOp",EDGE,"E305.filletArc"),sQuery(id+"F2.wireOp",EDGE,"E306.filletArc"),sQuery(id+"F2.wireOp",EDGE,"E307"),sQuery(id+"F2.wireOp",EDGE,"E308.MirrorCS"),sQuery(id+"F2.wireOp",EDGE,"E309.MirrorCS"),sQuery(id+"F2.wireOp",EDGE,"E310.MirrorCS"),sQuery(id+"F2.wireOp",EDGE,"E311.MirrorCS"),sQuery(id+"F2.wireOp",EDGE,"E312.MirrorCS"),sQuery(id+"F2.wireOp",EDGE,"E313.MirrorCS"),sQuery(id+"F2.wireOp",EDGE,"E314.MirrorCS"),sQuery(id+"F2.wireOp",EDGE,"E315.MirrorCS"),sQuery(id+"F2.wireOp",EDGE,"E316.MirrorCS"),sQuery(id+"F2.wireOp",EDGE,"E320.MirrorCS"),sQuery(id+"F2.wireOp",EDGE,"E321.MirrorCS"),sQuery(id+"F2.wireOp",EDGE,"E322.MirrorCS"),sQuery(id+"F2.wireOp",EDGE,"E323.MirrorCS"),sQuery(id+"F2.wireOp",EDGE,"E327.MirrorCS"),sQuery(id+"F2.wireOp",EDGE,"E328"),sQuery(id+"F2.wireOp",EDGE,"E329"),sQuery(id+"F2.wireOp",EDGE,"E330"),sQuery(id+"F2.wireOp",EDGE,"E331")])],"isStart":true})]});
            var sketch = newSketch(context, id + "F4", { "sketchPlane" : qUnion([Q0])});
            skLineSegment(sketch, "E332.bottom", {"start": v(-200, 2.5) * mm, "end": v(200, 2.5) * mm});
            skLineSegment(sketch, "E332.top", {"start": v(-200, -2.5) * mm, "end": v(200, -2.5) * mm});
            skLineSegment(sketch, "E332.left", {"start": v(-200, 2.5) * mm, "end": v(-200, -2.5) * mm});
            skLineSegment(sketch, "E332.right", {"start": v(200, 2.5) * mm, "end": v(200, -2.5) * mm});
            skLineSegment(sketch, "E333", {"start": v(-200, 0) * mm, "end": v(200, 0) * mm, "construction": true});
            skLineSegment(sketch, "E334.0.1.0", {"start": v(-200, 78.7) * mm, "end": v(200, 78.7) * mm});
            skLineSegment(sketch, "E334.0.1.1", {"start": v(-200, 73.7) * mm, "end": v(200, 73.7) * mm});
            skLineSegment(sketch, "E334.0.1.2", {"start": v(-200, 76.2) * mm, "end": v(200, 76.2) * mm, "construction": true});
            skLineSegment(sketch, "E334.0.1.3", {"start": v(200, 78.7) * mm, "end": v(200, 73.7) * mm});
            skLineSegment(sketch, "E334.0.1.4", {"start": v(-200, 78.7) * mm, "end": v(-200, 73.7) * mm});
            skLineSegment(sketch, "E334.direction1", {"start": v(-200, -2.5) * mm, "end": v(-176, -2.5) * mm, "construction": true});
            skLineSegment(sketch, "E334.direction2", {"start": v(-200, -2.5) * mm, "end": v(-200, 73.7) * mm, "construction": true});
            skLineSegment(sketch, "E335.0.1.0", {"start": v(-200, -78.7) * mm, "end": v(200, -78.7) * mm});
            skLineSegment(sketch, "E335.0.1.1", {"start": v(-200, -76.2) * mm, "end": v(200, -76.2) * mm, "construction": true});
            skLineSegment(sketch, "E335.0.1.2", {"start": v(-200, -78.7) * mm, "end": v(-176, -78.7) * mm, "construction": true});
            skLineSegment(sketch, "E335.0.1.3", {"start": v(-200, -73.7) * mm, "end": v(200, -73.7) * mm});
            skLineSegment(sketch, "E335.0.1.4", {"start": v(200, -73.7) * mm, "end": v(200, -78.7) * mm});
            skLineSegment(sketch, "E335.0.1.5", {"start": v(-200, -73.7) * mm, "end": v(-200, -78.7) * mm});
            skLineSegment(sketch, "E335.direction1", {"start": v(-200, -2.5) * mm, "end": v(-175, -2.5) * mm, "construction": true});
            skLineSegment(sketch, "E335.direction2", {"start": v(-200, -2.5) * mm, "end": v(-200, -78.7) * mm, "construction": true});
            skSolve(sketch);
        }
        {
            var Q0;
            Q0=makeQuery(id+"F4.imprint","IMPRINT",FACE,{"disambiguationData":[TD([[makeQuery(id+"F4.imprint","IMPRINT",EDGE,{"derivedFrom":sQuery(id+"F4.wireOp",EDGE,"E332.bottom")}),-1.0]])]});
            var Q1;
            {var subQ2=sQuery(id+"F4.wireOp",EDGE,"E334.0.1.0");Q1=makeQuery(id+"F4.imprint","IMPRINT",FACE,{"disambiguationData":[TD([[makeQuery(id+"F4.imprint","IMPRINT",EDGE,{"derivedFrom":subQ2}),-1.0]])]});}
            var Q2;
            {var subQ2=sQuery(id+"F4.wireOp",EDGE,"E335.0.1.0");Q2=makeQuery(id+"F4.imprint","IMPRINT",FACE,{"disambiguationData":[TD([[makeQuery(id+"F4.imprint","IMPRINT",EDGE,{"derivedFrom":subQ2}),1.0]])]});}
            extrude(context, id + "F5", {"entities" : qUnion([Q0, Q1, Q2]), "depth" : 30 * mm, "offsetDistance" : 25 * mm});
        }
        {
            var Q0;
            Q0=makeQuery(id+"F5.opExtrude","SWEPT_FACE",FACE,{"disambiguationData":[OSD([sQuery(id+"F4.wireOp",EDGE,"E335.0.1.0")])]});
            var sketch = newSketch(context, id + "F6", { "sketchPlane" : qUnion([Q0])});
            skLineSegment(sketch, "E336.bottom", {"start": v(-190, 35) * mm, "end": v(190, 35) * mm});
            skLineSegment(sketch, "E336.top", {"start": v(-175, 20) * mm, "end": v(175, 20) * mm});
            skLineSegment(sketch, "E336.left", {"start": v(-190, 35) * mm, "end": v(-190, 35) * mm});
            skLineSegment(sketch, "E336.right", {"start": v(190, 35) * mm, "end": v(190, 35) * mm});
            skPoint(sketch, "E337.visualSharp", {"position": v(-190, 20) * mm});
            skArc(sketch, "E337.filletArc", {"start": v(-190, 35) * mm, "mid": v(-185.6, 24.4) * mm, "end": v(-175, 20) * mm});
            skPoint(sketch, "E338.visualSharp", {"position": v(190, 20) * mm});
            skArc(sketch, "E338.filletArc", {"start": v(175, 20) * mm, "mid": v(185.6, 24.4) * mm, "end": v(190, 35) * mm});
            skSolve(sketch);
        }
        {
            var Q0;
            Q0=makeQuery(id+"F6.imprint","IMPRINT",FACE,{"disambiguationData":[TD([[makeQuery(id+"F6.imprint","IMPRINT",EDGE,{"derivedFrom":sQuery(id+"F6.wireOp",EDGE,"E336.bottom")}),-1.0]])]});
            extrude(context, id + "F7", {"entities" : qUnion([Q0]), "operationType" : NewBodyOperationType.REMOVE, "endBound" : BoundingType.THROUGH_ALL, "oppositeDirection" : true, "depth" : 25 * mm, "offsetDistance" : 25 * mm});
        }
        {
            var Q0;
            Q0=makeQuery(id+"F5.opExtrude","SWEPT_FACE",FACE,{"disambiguationData":[OSD([sQuery(id+"F4.wireOp",EDGE,"E335.0.1.0")])]});
            var sketch = newSketch(context, id + "F8", { "sketchPlane" : qUnion([Q0])});
            skLineSegment(sketch, "E339", {"start": v(0, 20) * mm, "end": v(0, 5) * mm, "construction": true});
            skLineSegment(sketch, "E340.0", {"start": v(-200, 35) * mm, "end": v(-200, 5) * mm});
            skLineSegment(sketch, "E341", {"start": v(-200, 10) * mm, "end": v(0, 10) * mm, "construction": true});
            skLineSegment(sketch, "E342.bottom", {"start": v(-47.25, 11.2) * mm, "end": v(-52.75, 11.2) * mm});
            skLineSegment(sketch, "E342.top", {"start": v(-47.25, 8.8) * mm, "end": v(-52.75, 8.8) * mm});
            skLineSegment(sketch, "E342.left", {"start": v(-47.25, 11.2) * mm, "end": v(-47.25, 8.8) * mm});
            skLineSegment(sketch, "E342.right", {"start": v(-52.75, 11.2) * mm, "end": v(-52.75, 8.8) * mm});
            skPoint(sketch, "E342.middle", {"position": v(-50, 10) * mm});
            skLineSegment(sketch, "E343.bottom", {"start": v(-51.6, 14) * mm, "end": v(-48.4, 14) * mm});
            skLineSegment(sketch, "E343.top", {"start": v(-51.6, 5) * mm, "end": v(-48.4, 5) * mm});
            skLineSegment(sketch, "E343.left", {"start": v(-51.6, 14) * mm, "end": v(-51.6, 5) * mm});
            skLineSegment(sketch, "E343.right", {"start": v(-48.4, 14) * mm, "end": v(-48.4, 5) * mm});
            skLineSegment(sketch, "E344", {"start": v(-50, 14) * mm, "end": v(-50, 5) * mm, "construction": true});
            skLineSegment(sketch, "E345", {"start": v(0, 5) * mm, "end": v(-107.96, 5) * mm, "construction": true});
            skLineSegment(sketch, "E346.1.0.0", {"start": v(-148.4, 14) * mm, "end": v(-148.4, 5) * mm});
            skLineSegment(sketch, "E346.1.0.1", {"start": v(-150, 14) * mm, "end": v(-150, 5) * mm, "construction": true});
            skLineSegment(sketch, "E346.1.0.2", {"start": v(-151.6, 14) * mm, "end": v(-151.6, 5) * mm});
            skPoint(sketch, "E346.1.0.3", {"position": v(-150, 10) * mm});
            skLineSegment(sketch, "E346.1.0.4", {"start": v(-147.25, 8.8) * mm, "end": v(-152.75, 8.8) * mm});
            skLineSegment(sketch, "E346.1.0.5", {"start": v(-151.6, 5) * mm, "end": v(-148.4, 5) * mm});
            skLineSegment(sketch, "E346.1.0.6", {"start": v(-147.25, 11.2) * mm, "end": v(-152.75, 11.2) * mm});
            skLineSegment(sketch, "E346.1.0.7", {"start": v(-151.6, 14) * mm, "end": v(-148.4, 14) * mm});
            skLineSegment(sketch, "E346.1.0.8", {"start": v(-152.75, 11.2) * mm, "end": v(-152.75, 8.8) * mm});
            skLineSegment(sketch, "E346.1.0.9", {"start": v(-147.25, 11.2) * mm, "end": v(-147.25, 8.8) * mm});
            skLineSegment(sketch, "E346.direction1", {"start": v(-51.6, 5) * mm, "end": v(-151.6, 5) * mm, "construction": true});
            skLineSegment(sketch, "E347", {"start": v(-195, 35) * mm, "end": v(-195, 5) * mm, "construction": true});
            skLineSegment(sketch, "E348.bottom", {"start": v(-193.8, 17.25) * mm, "end": v(-196.2, 17.25) * mm});
            skLineSegment(sketch, "E348.top", {"start": v(-193.8, 22.75) * mm, "end": v(-196.2, 22.75) * mm});
            skLineSegment(sketch, "E348.left", {"start": v(-193.8, 17.25) * mm, "end": v(-193.8, 22.75) * mm});
            skLineSegment(sketch, "E348.right", {"start": v(-196.2, 17.25) * mm, "end": v(-196.2, 22.75) * mm});
            skPoint(sketch, "E348.middle", {"position": v(-195, 20) * mm});
            skLineSegment(sketch, "E349.bottom", {"start": v(-200, 21.6) * mm, "end": v(-191, 21.6) * mm});
            skLineSegment(sketch, "E349.top", {"start": v(-200, 18.4) * mm, "end": v(-191, 18.4) * mm});
            skLineSegment(sketch, "E349.left", {"start": v(-200, 21.6) * mm, "end": v(-200, 18.4) * mm});
            skLineSegment(sketch, "E349.right", {"start": v(-191, 21.6) * mm, "end": v(-191, 18.4) * mm});
            skLineSegment(sketch, "E350", {"start": v(-200, 20) * mm, "end": v(-191, 20) * mm, "construction": true});
            skLineSegment(sketch, "E351.bottom", {"start": v(-26.75, 20) * mm, "end": v(-24.05, 20) * mm});
            skLineSegment(sketch, "E351.top", {"start": v(-26.75, 14) * mm, "end": v(-24.05, 14) * mm});
            skLineSegment(sketch, "E351.left", {"start": v(-26.75, 20) * mm, "end": v(-26.75, 14) * mm});
            skLineSegment(sketch, "E351.right", {"start": v(-24.05, 20) * mm, "end": v(-24.05, 14) * mm});
            skLineSegment(sketch, "E352.bottom", {"start": v(-22.9, 16) * mm, "end": v(-27.9, 16) * mm});
            skLineSegment(sketch, "E352.top", {"start": v(-22.9, 18) * mm, "end": v(-27.9, 18) * mm});
            skLineSegment(sketch, "E352.left", {"start": v(-22.9, 16) * mm, "end": v(-22.9, 18) * mm});
            skLineSegment(sketch, "E352.right", {"start": v(-27.9, 16) * mm, "end": v(-27.9, 18) * mm});
            skPoint(sketch, "E352.middle", {"position": v(-25.4, 17) * mm});
            skLineSegment(sketch, "E353", {"start": v(-25.4, 20) * mm, "end": v(-25.4, 14) * mm, "construction": true});
            skLineSegment(sketch, "E354.MirrorCS", {"start": v(26.75, 14) * mm, "end": v(24.05, 14) * mm});
            skLineSegment(sketch, "E355.MirrorCS", {"start": v(26.75, 20) * mm, "end": v(24.05, 20) * mm});
            skLineSegment(sketch, "E356.MirrorCS", {"start": v(25.4, 20) * mm, "end": v(25.4, 14) * mm, "construction": true});
            skLineSegment(sketch, "E357.MirrorCS", {"start": v(22.9, 16) * mm, "end": v(27.9, 16) * mm});
            skPoint(sketch, "E358.MirrorP", {"position": v(25.4, 17) * mm});
            skLineSegment(sketch, "E359.MirrorCS", {"start": v(26.75, 20) * mm, "end": v(26.75, 14) * mm});
            skLineSegment(sketch, "E360.MirrorCS", {"start": v(27.9, 16) * mm, "end": v(27.9, 18) * mm});
            skLineSegment(sketch, "E361.MirrorCS", {"start": v(22.9, 16) * mm, "end": v(22.9, 18) * mm});
            skLineSegment(sketch, "E362.MirrorCS", {"start": v(22.9, 18) * mm, "end": v(27.9, 18) * mm});
            skLineSegment(sketch, "E363.MirrorCS", {"start": v(24.05, 20) * mm, "end": v(24.05, 14) * mm});
            skLineSegment(sketch, "E364.MirrorCS", {"start": v(51.6, 14) * mm, "end": v(48.4, 14) * mm});
            skLineSegment(sketch, "E365.MirrorCS", {"start": v(47.25, 11.2) * mm, "end": v(52.75, 11.2) * mm});
            skLineSegment(sketch, "E366.MirrorCS", {"start": v(51.6, 5) * mm, "end": v(48.4, 5) * mm});
            skLineSegment(sketch, "E367.MirrorCS", {"start": v(51.6, 14) * mm, "end": v(51.6, 5) * mm});
            skLineSegment(sketch, "E368.MirrorCS", {"start": v(48.4, 14) * mm, "end": v(48.4, 5) * mm});
            skPoint(sketch, "E369.MirrorP", {"position": v(50, 10) * mm});
            skLineSegment(sketch, "E370.MirrorCS", {"start": v(47.25, 11.2) * mm, "end": v(47.25, 8.8) * mm});
            skLineSegment(sketch, "E371.MirrorCS", {"start": v(50, 14) * mm, "end": v(50, 5) * mm, "construction": true});
            skLineSegment(sketch, "E372.MirrorCS", {"start": v(52.75, 11.2) * mm, "end": v(52.75, 8.8) * mm});
            skLineSegment(sketch, "E373.MirrorCS", {"start": v(47.25, 8.8) * mm, "end": v(52.75, 8.8) * mm});
            skLineSegment(sketch, "E374.MirrorCS", {"start": v(147.25, 11.2) * mm, "end": v(147.25, 8.8) * mm});
            skLineSegment(sketch, "E375.MirrorCS", {"start": v(151.6, 14) * mm, "end": v(151.6, 5) * mm});
            skLineSegment(sketch, "E376.MirrorCS", {"start": v(151.6, 5) * mm, "end": v(148.4, 5) * mm});
            skPoint(sketch, "E377.MirrorP", {"position": v(150, 10) * mm});
            skLineSegment(sketch, "E378.MirrorCS", {"start": v(151.6, 14) * mm, "end": v(148.4, 14) * mm});
            skLineSegment(sketch, "E379.MirrorCS", {"start": v(147.25, 11.2) * mm, "end": v(152.75, 11.2) * mm});
            skLineSegment(sketch, "E380.MirrorCS", {"start": v(148.4, 14) * mm, "end": v(148.4, 5) * mm});
            skLineSegment(sketch, "E381.MirrorCS", {"start": v(152.75, 11.2) * mm, "end": v(152.75, 8.8) * mm});
            skLineSegment(sketch, "E382.MirrorCS", {"start": v(147.25, 8.8) * mm, "end": v(152.75, 8.8) * mm});
            skLineSegment(sketch, "E383.MirrorCS", {"start": v(150, 14) * mm, "end": v(150, 5) * mm, "construction": true});
            skLineSegment(sketch, "E384.MirrorCS", {"start": v(200, 21.6) * mm, "end": v(191, 21.6) * mm});
            skPoint(sketch, "E385.MirrorP", {"position": v(195, 20) * mm});
            skLineSegment(sketch, "E386.MirrorCS", {"start": v(193.8, 17.25) * mm, "end": v(196.2, 17.25) * mm});
            skLineSegment(sketch, "E387.MirrorCS", {"start": v(200, 20) * mm, "end": v(191, 20) * mm, "construction": true});
            skLineSegment(sketch, "E388.MirrorCS", {"start": v(200, 18.4) * mm, "end": v(191, 18.4) * mm});
            skLineSegment(sketch, "E389.MirrorCS", {"start": v(200, 21.6) * mm, "end": v(200, 18.4) * mm});
            skLineSegment(sketch, "E390.MirrorCS", {"start": v(193.8, 17.25) * mm, "end": v(193.8, 22.75) * mm});
            skLineSegment(sketch, "E391.MirrorCS", {"start": v(193.8, 22.75) * mm, "end": v(196.2, 22.75) * mm});
            skLineSegment(sketch, "E392.MirrorCS", {"start": v(196.2, 17.25) * mm, "end": v(196.2, 22.75) * mm});
            skLineSegment(sketch, "E393.MirrorCS", {"start": v(191, 21.6) * mm, "end": v(191, 18.4) * mm});
            skSolve(sketch);
        }
        {
            var Q0;
            {var subQ5=sQuery(id+"F8.wireOp",EDGE,"E349.left");Q0=makeQuery(id+"F8.imprint","IMPRINT",FACE,{"disambiguationData":[TD([[makeQuery(id+"F8.imprint","IMPRINT",EDGE,{"derivedFrom":subQ5}),1.0]])]});}
            var Q1;
            {var subQ0=sQuery(id+"F8.wireOp",EDGE,"E349.top");var subQ1=sQuery(id+"F8.wireOp",EDGE,"E348.left");var subQ2=makeQuery(id+"F8.imprint","INTERSECT",VERTEX,{"derivedFrom":[subQ1,subQ0]});Q1=makeQuery(id+"F8.imprint","IMPRINT",FACE,{"disambiguationData":[TD([[makeQuery(id+"F8.imprint","IMPRINT",EDGE,{"disambiguationData":[TD([[subQ2,-1.0]])],"derivedFrom":subQ1}),1.0]])]});}
            var Q2;
            {var subQ5=sQuery(id+"F8.wireOp",EDGE,"E349.right");Q2=makeQuery(id+"F8.imprint","IMPRINT",FACE,{"disambiguationData":[TD([[makeQuery(id+"F8.imprint","IMPRINT",EDGE,{"derivedFrom":subQ5}),-1.0]])]});}
            var Q3;
            {var subQ0=sQuery(id+"F8.wireOp",EDGE,"E348.top");Q3=makeQuery(id+"F8.imprint","IMPRINT",FACE,{"disambiguationData":[TD([[makeQuery(id+"F8.imprint","IMPRINT",EDGE,{"derivedFrom":subQ0}),1.0]])]});}
            var Q4;
            {var subQ0=sQuery(id+"F8.wireOp",EDGE,"E348.bottom");Q4=makeQuery(id+"F8.imprint","IMPRINT",FACE,{"disambiguationData":[TD([[makeQuery(id+"F8.imprint","IMPRINT",EDGE,{"derivedFrom":subQ0}),-1.0]])]});}
            var Q5;
            {var subQ0=sQuery(id+"F8.wireOp",EDGE,"E346.1.0.7");Q5=makeQuery(id+"F8.imprint","IMPRINT",FACE,{"disambiguationData":[TD([[makeQuery(id+"F8.imprint","IMPRINT",EDGE,{"derivedFrom":subQ0}),-1.0]])]});}
            var Q6;
            {var subQ0=sQuery(id+"F8.wireOp",EDGE,"E346.1.0.6");var subQ1=sQuery(id+"F8.wireOp",EDGE,"E346.1.0.0");var subQ2=makeQuery(id+"F8.imprint","INTERSECT",VERTEX,{"derivedFrom":[subQ1,subQ0]});Q6=makeQuery(id+"F8.imprint","IMPRINT",FACE,{"disambiguationData":[TD([[makeQuery(id+"F8.imprint","IMPRINT",EDGE,{"disambiguationData":[TD([[subQ2,-1.0]])],"derivedFrom":subQ1}),-1.0]])]});}
            var Q7;
            {var subQ0=sQuery(id+"F8.wireOp",EDGE,"E346.1.0.5");Q7=makeQuery(id+"F8.imprint","IMPRINT",FACE,{"disambiguationData":[TD([[makeQuery(id+"F8.imprint","IMPRINT",EDGE,{"derivedFrom":subQ0}),1.0]])]});}
            var Q8;
            {var subQ5=sQuery(id+"F8.wireOp",EDGE,"E346.1.0.8");Q8=makeQuery(id+"F8.imprint","IMPRINT",FACE,{"disambiguationData":[TD([[makeQuery(id+"F8.imprint","IMPRINT",EDGE,{"derivedFrom":subQ5}),1.0]])]});}
            var Q9;
            {var subQ5=sQuery(id+"F8.wireOp",EDGE,"E346.1.0.9");Q9=makeQuery(id+"F8.imprint","IMPRINT",FACE,{"disambiguationData":[TD([[makeQuery(id+"F8.imprint","IMPRINT",EDGE,{"derivedFrom":subQ5}),-1.0]])]});}
            var Q10;
            {var subQ0=sQuery(id+"F8.wireOp",EDGE,"E343.right");var subQ1=sQuery(id+"F8.wireOp",EDGE,"E342.bottom");var subQ2=makeQuery(id+"F8.imprint","INTERSECT",VERTEX,{"derivedFrom":[subQ1,subQ0]});Q10=makeQuery(id+"F8.imprint","IMPRINT",FACE,{"disambiguationData":[TD([[makeQuery(id+"F8.imprint","IMPRINT",EDGE,{"disambiguationData":[TD([[subQ2,-1.0]])],"derivedFrom":subQ1}),1.0]])]});}
            var Q11;
            {var subQ5=sQuery(id+"F8.wireOp",EDGE,"E343.bottom");Q11=makeQuery(id+"F8.imprint","IMPRINT",FACE,{"disambiguationData":[TD([[makeQuery(id+"F8.imprint","IMPRINT",EDGE,{"derivedFrom":subQ5}),-1.0]])]});}
            var Q12;
            {var subQ5=sQuery(id+"F8.wireOp",EDGE,"E343.top");Q12=makeQuery(id+"F8.imprint","IMPRINT",FACE,{"disambiguationData":[TD([[makeQuery(id+"F8.imprint","IMPRINT",EDGE,{"derivedFrom":subQ5}),1.0]])]});}
            var Q13;
            {var subQ0=sQuery(id+"F8.wireOp",EDGE,"E342.left");Q13=makeQuery(id+"F8.imprint","IMPRINT",FACE,{"disambiguationData":[TD([[makeQuery(id+"F8.imprint","IMPRINT",EDGE,{"derivedFrom":subQ0}),-1.0]])]});}
            var Q14;
            {var subQ0=sQuery(id+"F8.wireOp",EDGE,"E342.right");Q14=makeQuery(id+"F8.imprint","IMPRINT",FACE,{"disambiguationData":[TD([[makeQuery(id+"F8.imprint","IMPRINT",EDGE,{"derivedFrom":subQ0}),1.0]])]});}
            var Q15;
            {var subQ0=sQuery(id+"F8.wireOp",EDGE,"E351.bottom");Q15=makeQuery(id+"F8.imprint","IMPRINT",FACE,{"disambiguationData":[TD([[makeQuery(id+"F8.imprint","IMPRINT",EDGE,{"derivedFrom":subQ0}),-1.0]])]});}
            var Q16;
            {var subQ5=sQuery(id+"F8.wireOp",EDGE,"E352.right");Q16=makeQuery(id+"F8.imprint","IMPRINT",FACE,{"disambiguationData":[TD([[makeQuery(id+"F8.imprint","IMPRINT",EDGE,{"derivedFrom":subQ5}),-1.0]])]});}
            var Q17;
            {var subQ5=sQuery(id+"F8.wireOp",EDGE,"E352.left");Q17=makeQuery(id+"F8.imprint","IMPRINT",FACE,{"disambiguationData":[TD([[makeQuery(id+"F8.imprint","IMPRINT",EDGE,{"derivedFrom":subQ5}),1.0]])]});}
            var Q18;
            {var subQ0=sQuery(id+"F8.wireOp",EDGE,"E351.top");Q18=makeQuery(id+"F8.imprint","IMPRINT",FACE,{"disambiguationData":[TD([[makeQuery(id+"F8.imprint","IMPRINT",EDGE,{"derivedFrom":subQ0}),1.0]])]});}
            var Q19;
            {var subQ0=sQuery(id+"F8.wireOp",EDGE,"E352.top");var subQ1=sQuery(id+"F8.wireOp",EDGE,"E351.left");var subQ2=makeQuery(id+"F8.imprint","INTERSECT",VERTEX,{"derivedFrom":[subQ1,subQ0]});Q19=makeQuery(id+"F8.imprint","IMPRINT",FACE,{"disambiguationData":[TD([[makeQuery(id+"F8.imprint","IMPRINT",EDGE,{"disambiguationData":[TD([[subQ2,-1.0]])],"derivedFrom":subQ1}),1.0]])]});}
            var Q20;
            {var subQ0=sQuery(id+"F8.wireOp",EDGE,"E355.MirrorCS");Q20=makeQuery(id+"F8.imprint","IMPRINT",FACE,{"disambiguationData":[TD([[makeQuery(id+"F8.imprint","IMPRINT",EDGE,{"derivedFrom":subQ0}),-1.0]])]});}
            var Q21;
            {var subQ0=sQuery(id+"F8.wireOp",EDGE,"E363.MirrorCS");var subQ1=sQuery(id+"F8.wireOp",EDGE,"E357.MirrorCS");var subQ2=makeQuery(id+"F8.imprint","INTERSECT",VERTEX,{"derivedFrom":[subQ1,subQ0]});Q21=makeQuery(id+"F8.imprint","IMPRINT",FACE,{"disambiguationData":[TD([[makeQuery(id+"F8.imprint","IMPRINT",EDGE,{"disambiguationData":[TD([[subQ2,-1.0]])],"derivedFrom":subQ1}),1.0]])]});}
            var Q22;
            {var subQ0=sQuery(id+"F8.wireOp",EDGE,"E361.MirrorCS");Q22=makeQuery(id+"F8.imprint","IMPRINT",FACE,{"disambiguationData":[TD([[makeQuery(id+"F8.imprint","IMPRINT",EDGE,{"derivedFrom":subQ0}),-1.0]])]});}
            var Q23;
            {var subQ0=sQuery(id+"F8.wireOp",EDGE,"E354.MirrorCS");Q23=makeQuery(id+"F8.imprint","IMPRINT",FACE,{"disambiguationData":[TD([[makeQuery(id+"F8.imprint","IMPRINT",EDGE,{"derivedFrom":subQ0}),-1.0]])]});}
            var Q24;
            {var subQ0=sQuery(id+"F8.wireOp",EDGE,"E360.MirrorCS");Q24=makeQuery(id+"F8.imprint","IMPRINT",FACE,{"disambiguationData":[TD([[makeQuery(id+"F8.imprint","IMPRINT",EDGE,{"derivedFrom":subQ0}),1.0]])]});}
            var Q25;
            {var subQ0=sQuery(id+"F8.wireOp",EDGE,"E364.MirrorCS");Q25=makeQuery(id+"F8.imprint","IMPRINT",FACE,{"disambiguationData":[TD([[makeQuery(id+"F8.imprint","IMPRINT",EDGE,{"derivedFrom":subQ0}),1.0]])]});}
            var Q26;
            {var subQ0=sQuery(id+"F8.wireOp",EDGE,"E368.MirrorCS");var subQ1=sQuery(id+"F8.wireOp",EDGE,"E365.MirrorCS");var subQ2=makeQuery(id+"F8.imprint","INTERSECT",VERTEX,{"derivedFrom":[subQ1,subQ0]});Q26=makeQuery(id+"F8.imprint","IMPRINT",FACE,{"disambiguationData":[TD([[makeQuery(id+"F8.imprint","IMPRINT",EDGE,{"disambiguationData":[TD([[subQ2,-1.0]])],"derivedFrom":subQ1}),-1.0]])]});}
            var Q27;
            {var subQ0=sQuery(id+"F8.wireOp",EDGE,"E366.MirrorCS");Q27=makeQuery(id+"F8.imprint","IMPRINT",FACE,{"disambiguationData":[TD([[makeQuery(id+"F8.imprint","IMPRINT",EDGE,{"derivedFrom":subQ0}),1.0]])]});}
            var Q28;
            {var subQ0=sQuery(id+"F8.wireOp",EDGE,"E372.MirrorCS");Q28=makeQuery(id+"F8.imprint","IMPRINT",FACE,{"disambiguationData":[TD([[makeQuery(id+"F8.imprint","IMPRINT",EDGE,{"derivedFrom":subQ0}),-1.0]])]});}
            var Q29;
            {var subQ0=sQuery(id+"F8.wireOp",EDGE,"E370.MirrorCS");Q29=makeQuery(id+"F8.imprint","IMPRINT",FACE,{"disambiguationData":[TD([[makeQuery(id+"F8.imprint","IMPRINT",EDGE,{"derivedFrom":subQ0}),1.0]])]});}
            var Q30;
            {var subQ0=sQuery(id+"F8.wireOp",EDGE,"E379.MirrorCS");var subQ1=sQuery(id+"F8.wireOp",EDGE,"E375.MirrorCS");var subQ2=makeQuery(id+"F8.imprint","INTERSECT",VERTEX,{"derivedFrom":[subQ1,subQ0]});Q30=makeQuery(id+"F8.imprint","IMPRINT",FACE,{"disambiguationData":[TD([[makeQuery(id+"F8.imprint","IMPRINT",EDGE,{"disambiguationData":[TD([[subQ2,-1.0]])],"derivedFrom":subQ1}),-1.0]])]});}
            var Q31;
            {var subQ0=sQuery(id+"F8.wireOp",EDGE,"E378.MirrorCS");Q31=makeQuery(id+"F8.imprint","IMPRINT",FACE,{"disambiguationData":[TD([[makeQuery(id+"F8.imprint","IMPRINT",EDGE,{"derivedFrom":subQ0}),1.0]])]});}
            var Q32;
            {var subQ0=sQuery(id+"F8.wireOp",EDGE,"E376.MirrorCS");Q32=makeQuery(id+"F8.imprint","IMPRINT",FACE,{"disambiguationData":[TD([[makeQuery(id+"F8.imprint","IMPRINT",EDGE,{"derivedFrom":subQ0}),1.0]])]});}
            var Q33;
            {var subQ0=sQuery(id+"F8.wireOp",EDGE,"E374.MirrorCS");Q33=makeQuery(id+"F8.imprint","IMPRINT",FACE,{"disambiguationData":[TD([[makeQuery(id+"F8.imprint","IMPRINT",EDGE,{"derivedFrom":subQ0}),1.0]])]});}
            var Q34;
            {var subQ5=sQuery(id+"F8.wireOp",EDGE,"E381.MirrorCS");Q34=makeQuery(id+"F8.imprint","IMPRINT",FACE,{"disambiguationData":[TD([[makeQuery(id+"F8.imprint","IMPRINT",EDGE,{"derivedFrom":subQ5}),-1.0]])]});}
            var Q35;
            {var subQ0=sQuery(id+"F8.wireOp",EDGE,"E389.MirrorCS");Q35=makeQuery(id+"F8.imprint","IMPRINT",FACE,{"disambiguationData":[TD([[makeQuery(id+"F8.imprint","IMPRINT",EDGE,{"derivedFrom":subQ0}),-1.0]])]});}
            var Q36;
            {var subQ0=sQuery(id+"F8.wireOp",EDGE,"E392.MirrorCS");var subQ1=sQuery(id+"F8.wireOp",EDGE,"E384.MirrorCS");var subQ2=makeQuery(id+"F8.imprint","INTERSECT",VERTEX,{"derivedFrom":[subQ1,subQ0]});Q36=makeQuery(id+"F8.imprint","IMPRINT",FACE,{"disambiguationData":[TD([[makeQuery(id+"F8.imprint","IMPRINT",EDGE,{"disambiguationData":[TD([[subQ2,-1.0]])],"derivedFrom":subQ1}),1.0]])]});}
            var Q37;
            {var subQ5=sQuery(id+"F8.wireOp",EDGE,"E391.MirrorCS");Q37=makeQuery(id+"F8.imprint","IMPRINT",FACE,{"disambiguationData":[TD([[makeQuery(id+"F8.imprint","IMPRINT",EDGE,{"derivedFrom":subQ5}),-1.0]])]});}
            var Q38;
            {var subQ0=sQuery(id+"F8.wireOp",EDGE,"E386.MirrorCS");Q38=makeQuery(id+"F8.imprint","IMPRINT",FACE,{"disambiguationData":[TD([[makeQuery(id+"F8.imprint","IMPRINT",EDGE,{"derivedFrom":subQ0}),1.0]])]});}
            var Q39;
            {var subQ0=sQuery(id+"F8.wireOp",EDGE,"E393.MirrorCS");Q39=makeQuery(id+"F8.imprint","IMPRINT",FACE,{"disambiguationData":[TD([[makeQuery(id+"F8.imprint","IMPRINT",EDGE,{"derivedFrom":subQ0}),1.0]])]});}
            extrude(context, id + "F9", {"entities" : qUnion([Q0, Q1, Q2, Q3, Q4, Q5, Q6, Q7, Q8, Q9, Q10, Q11, Q12, Q13, Q14, Q15, Q16, Q17, Q18, Q19, Q20, Q21, Q22, Q23, Q24, Q25, Q26, Q27, Q28, Q29, Q30, Q31, Q32, Q33, Q34, Q35, Q36, Q37, Q38, Q39]), "operationType" : NewBodyOperationType.REMOVE, "endBound" : BoundingType.THROUGH_ALL, "oppositeDirection" : true, "depth" : 25 * mm, "offsetDistance" : 25 * mm});
        }
        {
            var Q0;
            Q0=makeQuery(id+"F3.boolean.opBoolean","MERGE",FACE,{"derivedFrom":[makeQuery(id+"F1.opExtrude","CAP_FACE",FACE,{"disambiguationData":[OSD([sQuery(id+"F0.wireOp",EDGE,"E0"),sQuery(id+"F0.wireOp",EDGE,"E1"),sQuery(id+"F0.wireOp",EDGE,"E2"),sQuery(id+"F0.wireOp",EDGE,"E3"),sQuery(id+"F0.wireOp",EDGE,"E4"),sQuery(id+"F0.wireOp",EDGE,"E5"),sQuery(id+"F0.wireOp",EDGE,"E6"),sQuery(id+"F0.wireOp",EDGE,"E7"),sQuery(id+"F0.wireOp",EDGE,"E8"),sQuery(id+"F0.wireOp",EDGE,"E9"),sQuery(id+"F0.wireOp",EDGE,"E10"),sQuery(id+"F0.wireOp",EDGE,"E11"),sQuery(id+"F0.wireOp",EDGE,"E12"),sQuery(id+"F0.wireOp",EDGE,"E13"),sQuery(id+"F0.wireOp",EDGE,"E14"),sQuery(id+"F0.wireOp",EDGE,"E15"),sQuery(id+"F0.wireOp",EDGE,"E16"),sQuery(id+"F0.wireOp",EDGE,"E17"),sQuery(id+"F0.wireOp",EDGE,"E18"),sQuery(id+"F0.wireOp",EDGE,"E19"),sQuery(id+"F0.wireOp",EDGE,"E20"),sQuery(id+"F0.wireOp",EDGE,"E21"),sQuery(id+"F0.wireOp",EDGE,"E22"),sQuery(id+"F0.wireOp",EDGE,"E23"),sQuery(id+"F0.wireOp",EDGE,"E24"),sQuery(id+"F0.wireOp",EDGE,"E25"),sQuery(id+"F0.wireOp",EDGE,"E26"),sQuery(id+"F0.wireOp",EDGE,"E27"),sQuery(id+"F0.wireOp",EDGE,"E28"),sQuery(id+"F0.wireOp",EDGE,"E29"),sQuery(id+"F0.wireOp",EDGE,"E30"),sQuery(id+"F0.wireOp",EDGE,"E31"),sQuery(id+"F0.wireOp",EDGE,"E32"),sQuery(id+"F0.wireOp",EDGE,"E33"),sQuery(id+"F0.wireOp",EDGE,"E34"),sQuery(id+"F0.wireOp",EDGE,"E35"),sQuery(id+"F0.wireOp",EDGE,"E36"),sQuery(id+"F0.wireOp",EDGE,"E37"),sQuery(id+"F0.wireOp",EDGE,"E38"),sQuery(id+"F0.wireOp",EDGE,"E39"),sQuery(id+"F0.wireOp",EDGE,"E40"),sQuery(id+"F0.wireOp",EDGE,"E41"),sQuery(id+"F0.wireOp",EDGE,"E42"),sQuery(id+"F0.wireOp",EDGE,"E43"),sQuery(id+"F0.wireOp",EDGE,"E44"),sQuery(id+"F0.wireOp",EDGE,"E45"),sQuery(id+"F0.wireOp",EDGE,"E46"),sQuery(id+"F0.wireOp",EDGE,"E47"),sQuery(id+"F0.wireOp",EDGE,"E48"),sQuery(id+"F0.wireOp",EDGE,"E49"),sQuery(id+"F0.wireOp",EDGE,"E50"),sQuery(id+"F0.wireOp",EDGE,"E51"),sQuery(id+"F0.wireOp",EDGE,"E52"),sQuery(id+"F0.wireOp",EDGE,"E53"),sQuery(id+"F0.wireOp",EDGE,"E54"),sQuery(id+"F0.wireOp",EDGE,"E55"),sQuery(id+"F0.wireOp",EDGE,"E56"),sQuery(id+"F0.wireOp",EDGE,"E57"),sQuery(id+"F0.wireOp",EDGE,"E58"),sQuery(id+"F0.wireOp",EDGE,"E59"),sQuery(id+"F0.wireOp",EDGE,"E60"),sQuery(id+"F0.wireOp",EDGE,"E61"),sQuery(id+"F0.wireOp",EDGE,"E62"),sQuery(id+"F0.wireOp",EDGE,"E63"),sQuery(id+"F0.wireOp",EDGE,"E64"),sQuery(id+"F0.wireOp",EDGE,"E65"),sQuery(id+"F0.wireOp",EDGE,"E66"),sQuery(id+"F0.wireOp",EDGE,"E67"),sQuery(id+"F0.wireOp",EDGE,"E68"),sQuery(id+"F0.wireOp",EDGE,"E69"),sQuery(id+"F0.wireOp",EDGE,"E70"),sQuery(id+"F0.wireOp",EDGE,"E71"),sQuery(id+"F0.wireOp",EDGE,"E72"),sQuery(id+"F0.wireOp",EDGE,"E73"),sQuery(id+"F0.wireOp",EDGE,"E74"),sQuery(id+"F0.wireOp",EDGE,"E75"),sQuery(id+"F0.wireOp",EDGE,"E76"),sQuery(id+"F0.wireOp",EDGE,"E77"),sQuery(id+"F0.wireOp",EDGE,"E78"),sQuery(id+"F0.wireOp",EDGE,"E79"),sQuery(id+"F0.wireOp",EDGE,"E80"),sQuery(id+"F0.wireOp",EDGE,"E81"),sQuery(id+"F0.wireOp",EDGE,"E82"),sQuery(id+"F0.wireOp",EDGE,"E83"),sQuery(id+"F0.wireOp",EDGE,"E84"),sQuery(id+"F0.wireOp",EDGE,"E85"),sQuery(id+"F0.wireOp",EDGE,"E86"),sQuery(id+"F0.wireOp",EDGE,"E87"),sQuery(id+"F0.wireOp",EDGE,"E88"),sQuery(id+"F0.wireOp",EDGE,"E89"),sQuery(id+"F0.wireOp",EDGE,"E90"),sQuery(id+"F0.wireOp",EDGE,"E91"),sQuery(id+"F0.wireOp",EDGE,"E92"),sQuery(id+"F0.wireOp",EDGE,"E93"),sQuery(id+"F0.wireOp",EDGE,"E94"),sQuery(id+"F0.wireOp",EDGE,"E95"),sQuery(id+"F0.wireOp",EDGE,"E96"),sQuery(id+"F0.wireOp",EDGE,"E97"),sQuery(id+"F0.wireOp",EDGE,"E98"),sQuery(id+"F0.wireOp",EDGE,"E99"),sQuery(id+"F0.wireOp",EDGE,"E100"),sQuery(id+"F0.wireOp",EDGE,"E101"),sQuery(id+"F0.wireOp",EDGE,"E102"),sQuery(id+"F0.wireOp",EDGE,"E103"),sQuery(id+"F0.wireOp",EDGE,"E104"),sQuery(id+"F0.wireOp",EDGE,"E105"),sQuery(id+"F0.wireOp",EDGE,"E106"),sQuery(id+"F0.wireOp",EDGE,"E107"),sQuery(id+"F0.wireOp",EDGE,"E108"),sQuery(id+"F0.wireOp",EDGE,"E109"),sQuery(id+"F0.wireOp",EDGE,"E110"),sQuery(id+"F0.wireOp",EDGE,"E111"),sQuery(id+"F0.wireOp",EDGE,"E112"),sQuery(id+"F0.wireOp",EDGE,"E113"),sQuery(id+"F0.wireOp",EDGE,"E114"),sQuery(id+"F0.wireOp",EDGE,"E115"),sQuery(id+"F0.wireOp",EDGE,"E116"),sQuery(id+"F0.wireOp",EDGE,"E117"),sQuery(id+"F0.wireOp",EDGE,"E118"),sQuery(id+"F0.wireOp",EDGE,"E119"),sQuery(id+"F0.wireOp",EDGE,"E120"),sQuery(id+"F0.wireOp",EDGE,"E121"),sQuery(id+"F0.wireOp",EDGE,"E122"),sQuery(id+"F0.wireOp",EDGE,"E123"),sQuery(id+"F0.wireOp",EDGE,"E124"),sQuery(id+"F0.wireOp",EDGE,"E125"),sQuery(id+"F0.wireOp",EDGE,"E126"),sQuery(id+"F0.wireOp",EDGE,"E127"),sQuery(id+"F0.wireOp",EDGE,"E128"),sQuery(id+"F0.wireOp",EDGE,"E129"),sQuery(id+"F0.wireOp",EDGE,"E130"),sQuery(id+"F0.wireOp",EDGE,"E131"),sQuery(id+"F0.wireOp",EDGE,"E132"),sQuery(id+"F0.wireOp",EDGE,"E133"),sQuery(id+"F0.wireOp",EDGE,"E134"),sQuery(id+"F0.wireOp",EDGE,"E135"),sQuery(id+"F0.wireOp",EDGE,"E136"),sQuery(id+"F0.wireOp",EDGE,"E137"),sQuery(id+"F0.wireOp",EDGE,"E138"),sQuery(id+"F0.wireOp",EDGE,"E139"),sQuery(id+"F0.wireOp",EDGE,"E140"),sQuery(id+"F0.wireOp",EDGE,"E141"),sQuery(id+"F0.wireOp",EDGE,"E142"),sQuery(id+"F0.wireOp",EDGE,"E143"),sQuery(id+"F0.wireOp",EDGE,"E144"),sQuery(id+"F0.wireOp",EDGE,"E145"),sQuery(id+"F0.wireOp",EDGE,"E146"),sQuery(id+"F0.wireOp",EDGE,"E147"),sQuery(id+"F0.wireOp",EDGE,"E148"),sQuery(id+"F0.wireOp",EDGE,"E149"),sQuery(id+"F0.wireOp",EDGE,"E150"),sQuery(id+"F0.wireOp",EDGE,"E151"),sQuery(id+"F0.wireOp",EDGE,"E152"),sQuery(id+"F0.wireOp",EDGE,"E153"),sQuery(id+"F0.wireOp",EDGE,"E154"),sQuery(id+"F0.wireOp",EDGE,"E155"),sQuery(id+"F0.wireOp",EDGE,"E156"),sQuery(id+"F0.wireOp",EDGE,"E157"),sQuery(id+"F0.wireOp",EDGE,"E158"),sQuery(id+"F0.wireOp",EDGE,"E159"),sQuery(id+"F0.wireOp",EDGE,"E160"),sQuery(id+"F0.wireOp",EDGE,"E161"),sQuery(id+"F0.wireOp",EDGE,"E162"),sQuery(id+"F0.wireOp",EDGE,"E163"),sQuery(id+"F0.wireOp",EDGE,"E164"),sQuery(id+"F0.wireOp",EDGE,"E165"),sQuery(id+"F0.wireOp",EDGE,"E166"),sQuery(id+"F0.wireOp",EDGE,"E167"),sQuery(id+"F0.wireOp",EDGE,"E168"),sQuery(id+"F0.wireOp",EDGE,"E169"),sQuery(id+"F0.wireOp",EDGE,"E170"),sQuery(id+"F0.wireOp",EDGE,"E171"),sQuery(id+"F0.wireOp",EDGE,"E172"),sQuery(id+"F0.wireOp",EDGE,"E173"),sQuery(id+"F0.wireOp",EDGE,"E174"),sQuery(id+"F0.wireOp",EDGE,"E175"),sQuery(id+"F0.wireOp",EDGE,"E176"),sQuery(id+"F0.wireOp",EDGE,"E177"),sQuery(id+"F0.wireOp",EDGE,"E178"),sQuery(id+"F0.wireOp",EDGE,"E179"),sQuery(id+"F0.wireOp",EDGE,"E180"),sQuery(id+"F0.wireOp",EDGE,"E181"),sQuery(id+"F0.wireOp",EDGE,"E182"),sQuery(id+"F0.wireOp",EDGE,"E183"),sQuery(id+"F0.wireOp",EDGE,"E184"),sQuery(id+"F0.wireOp",EDGE,"E185"),sQuery(id+"F0.wireOp",EDGE,"E186"),sQuery(id+"F0.wireOp",EDGE,"E187"),sQuery(id+"F0.wireOp",EDGE,"E188"),sQuery(id+"F0.wireOp",EDGE,"E189"),sQuery(id+"F0.wireOp",EDGE,"E190"),sQuery(id+"F0.wireOp",EDGE,"E191"),sQuery(id+"F0.wireOp",EDGE,"E192"),sQuery(id+"F0.wireOp",EDGE,"E193"),sQuery(id+"F0.wireOp",EDGE,"E194"),sQuery(id+"F0.wireOp",EDGE,"E195"),sQuery(id+"F0.wireOp",EDGE,"E196"),sQuery(id+"F0.wireOp",EDGE,"E197"),sQuery(id+"F0.wireOp",EDGE,"E198"),sQuery(id+"F0.wireOp",EDGE,"E199"),sQuery(id+"F0.wireOp",EDGE,"E200"),sQuery(id+"F0.wireOp",EDGE,"E201"),sQuery(id+"F0.wireOp",EDGE,"E202"),sQuery(id+"F0.wireOp",EDGE,"E203"),sQuery(id+"F0.wireOp",EDGE,"E204"),sQuery(id+"F0.wireOp",EDGE,"E205"),sQuery(id+"F0.wireOp",EDGE,"E206"),sQuery(id+"F0.wireOp",EDGE,"E207"),sQuery(id+"F0.wireOp",EDGE,"E208"),sQuery(id+"F0.wireOp",EDGE,"E209"),sQuery(id+"F0.wireOp",EDGE,"E210"),sQuery(id+"F0.wireOp",EDGE,"E211"),sQuery(id+"F0.wireOp",EDGE,"E212"),sQuery(id+"F0.wireOp",EDGE,"E213"),sQuery(id+"F0.wireOp",EDGE,"E214"),sQuery(id+"F0.wireOp",EDGE,"E215"),sQuery(id+"F0.wireOp",EDGE,"E216"),sQuery(id+"F0.wireOp",EDGE,"E217"),sQuery(id+"F0.wireOp",EDGE,"E218"),sQuery(id+"F0.wireOp",EDGE,"E219"),sQuery(id+"F0.wireOp",EDGE,"E220"),sQuery(id+"F0.wireOp",EDGE,"E221"),sQuery(id+"F0.wireOp",EDGE,"E222"),sQuery(id+"F0.wireOp",EDGE,"E223"),sQuery(id+"F0.wireOp",EDGE,"E224"),sQuery(id+"F0.wireOp",EDGE,"E225"),sQuery(id+"F0.wireOp",EDGE,"E226"),sQuery(id+"F0.wireOp",EDGE,"E227"),sQuery(id+"F0.wireOp",EDGE,"E228"),sQuery(id+"F0.wireOp",EDGE,"E229"),sQuery(id+"F0.wireOp",EDGE,"E230"),sQuery(id+"F0.wireOp",EDGE,"E231"),sQuery(id+"F0.wireOp",EDGE,"E232"),sQuery(id+"F0.wireOp",EDGE,"E233"),sQuery(id+"F0.wireOp",EDGE,"E234"),sQuery(id+"F0.wireOp",EDGE,"E235"),sQuery(id+"F0.wireOp",EDGE,"E236"),sQuery(id+"F0.wireOp",EDGE,"E237"),sQuery(id+"F0.wireOp",EDGE,"E238"),sQuery(id+"F0.wireOp",EDGE,"E239"),sQuery(id+"F0.wireOp",EDGE,"E240"),sQuery(id+"F0.wireOp",EDGE,"E241"),sQuery(id+"F0.wireOp",EDGE,"E242"),sQuery(id+"F0.wireOp",EDGE,"E243"),sQuery(id+"F0.wireOp",EDGE,"E244"),sQuery(id+"F0.wireOp",EDGE,"E245"),sQuery(id+"F0.wireOp",EDGE,"E246"),sQuery(id+"F0.wireOp",EDGE,"E247"),sQuery(id+"F0.wireOp",EDGE,"E248"),sQuery(id+"F0.wireOp",EDGE,"E249"),sQuery(id+"F0.wireOp",EDGE,"E250"),sQuery(id+"F0.wireOp",EDGE,"E251"),sQuery(id+"F0.wireOp",EDGE,"E252"),sQuery(id+"F0.wireOp",EDGE,"E253"),sQuery(id+"F0.wireOp",EDGE,"E254"),sQuery(id+"F0.wireOp",EDGE,"E255"),sQuery(id+"F0.wireOp",EDGE,"E256"),sQuery(id+"F0.wireOp",EDGE,"E257"),sQuery(id+"F0.wireOp",EDGE,"E258"),sQuery(id+"F0.wireOp",EDGE,"E259"),sQuery(id+"F0.wireOp",EDGE,"E260"),sQuery(id+"F0.wireOp",EDGE,"E261"),sQuery(id+"F0.wireOp",EDGE,"E262"),sQuery(id+"F0.wireOp",EDGE,"E263"),sQuery(id+"F0.wireOp",EDGE,"E264"),sQuery(id+"F0.wireOp",EDGE,"E265"),sQuery(id+"F0.wireOp",EDGE,"E266"),sQuery(id+"F0.wireOp",EDGE,"E267"),sQuery(id+"F0.wireOp",EDGE,"E268"),sQuery(id+"F0.wireOp",EDGE,"E269"),sQuery(id+"F0.wireOp",EDGE,"E270"),sQuery(id+"F0.wireOp",EDGE,"E271"),sQuery(id+"F0.wireOp",EDGE,"E272"),sQuery(id+"F0.wireOp",EDGE,"E273"),sQuery(id+"F0.wireOp",EDGE,"E274"),sQuery(id+"F0.wireOp",EDGE,"E275"),sQuery(id+"F0.wireOp",EDGE,"E276"),sQuery(id+"F0.wireOp",EDGE,"E277"),sQuery(id+"F0.wireOp",EDGE,"E278"),sQuery(id+"F0.wireOp",EDGE,"E279"),sQuery(id+"F0.wireOp",EDGE,"E280"),sQuery(id+"F0.wireOp",EDGE,"E281"),sQuery(id+"F0.wireOp",EDGE,"E282"),sQuery(id+"F0.wireOp",EDGE,"E283"),sQuery(id+"F0.wireOp",EDGE,"E284"),sQuery(id+"F0.wireOp",EDGE,"E285"),sQuery(id+"F0.wireOp",EDGE,"E286"),sQuery(id+"F0.wireOp",EDGE,"E287"),sQuery(id+"F0.wireOp",EDGE,"E288"),sQuery(id+"F0.wireOp",EDGE,"E289"),sQuery(id+"F0.wireOp",EDGE,"E290"),sQuery(id+"F0.wireOp",EDGE,"E291")])],"isStart":true}),makeQuery(id+"F3.opExtrude","CAP_FACE",FACE,{"disambiguationData":[OSD([sQuery(id+"F2.wireOp",EDGE,"E294"),sQuery(id+"F2.wireOp",EDGE,"E295"),sQuery(id+"F2.wireOp",EDGE,"E296"),sQuery(id+"F2.wireOp",EDGE,"E297"),sQuery(id+"F2.wireOp",EDGE,"E298"),sQuery(id+"F2.wireOp",EDGE,"E299"),sQuery(id+"F2.wireOp",EDGE,"E300"),sQuery(id+"F2.wireOp",EDGE,"E301.filletArc"),sQuery(id+"F2.wireOp",EDGE,"E302.filletArc"),sQuery(id+"F2.wireOp",EDGE,"E303.filletArc"),sQuery(id+"F2.wireOp",EDGE,"E304.filletArc"),sQuery(id+"F2.wireOp",EDGE,"E305.filletArc"),sQuery(id+"F2.wireOp",EDGE,"E306.filletArc"),sQuery(id+"F2.wireOp",EDGE,"E307"),sQuery(id+"F2.wireOp",EDGE,"E308.MirrorCS"),sQuery(id+"F2.wireOp",EDGE,"E309.MirrorCS"),sQuery(id+"F2.wireOp",EDGE,"E310.MirrorCS"),sQuery(id+"F2.wireOp",EDGE,"E311.MirrorCS"),sQuery(id+"F2.wireOp",EDGE,"E312.MirrorCS"),sQuery(id+"F2.wireOp",EDGE,"E313.MirrorCS"),sQuery(id+"F2.wireOp",EDGE,"E314.MirrorCS"),sQuery(id+"F2.wireOp",EDGE,"E315.MirrorCS"),sQuery(id+"F2.wireOp",EDGE,"E316.MirrorCS"),sQuery(id+"F2.wireOp",EDGE,"E320.MirrorCS"),sQuery(id+"F2.wireOp",EDGE,"E321.MirrorCS"),sQuery(id+"F2.wireOp",EDGE,"E322.MirrorCS"),sQuery(id+"F2.wireOp",EDGE,"E323.MirrorCS"),sQuery(id+"F2.wireOp",EDGE,"E327.MirrorCS"),sQuery(id+"F2.wireOp",EDGE,"E328"),sQuery(id+"F2.wireOp",EDGE,"E329"),sQuery(id+"F2.wireOp",EDGE,"E330"),sQuery(id+"F2.wireOp",EDGE,"E331")])],"isStart":false})]});
            var sketch = newSketch(context, id + "F10", { "sketchPlane" : qUnion([Q0])});
            skPoint(sketch, "E394.0", {"position": v(-150, 78.7) * mm});
            skPoint(sketch, "E395.0", {"position": v(-151.6, 76.2) * mm});
            skLineSegment(sketch, "E396", {"start": v(-150, 78.7) * mm, "end": v(-150, 76.2) * mm, "construction": true});
            skLineSegment(sketch, "E397", {"start": v(-151.6, 76.2) * mm, "end": v(-150, 76.2) * mm, "construction": true});
            skLineSegment(sketch, "E398.0.1.0", {"start": v(-150, 2.5) * mm, "end": v(-150, 0) * mm, "construction": true});
            skLineSegment(sketch, "E398.0.2.0", {"start": v(-150, -73.7) * mm, "end": v(-150, -76.2) * mm, "construction": true});
            skLineSegment(sketch, "E398.1.0.0", {"start": v(-50, 78.7) * mm, "end": v(-50, 76.2) * mm, "construction": true});
            skLineSegment(sketch, "E398.1.1.0", {"start": v(-50, 2.5) * mm, "end": v(-50, 0) * mm, "construction": true});
            skLineSegment(sketch, "E398.1.2.0", {"start": v(-50, -73.7) * mm, "end": v(-50, -76.2) * mm, "construction": true});
            skLineSegment(sketch, "E398.2.0.0", {"start": v(50, 78.7) * mm, "end": v(50, 76.2) * mm, "construction": true});
            skLineSegment(sketch, "E398.2.1.0", {"start": v(50, 2.5) * mm, "end": v(50, 0) * mm, "construction": true});
            skLineSegment(sketch, "E398.2.2.0", {"start": v(50, -73.7) * mm, "end": v(50, -76.2) * mm, "construction": true});
            skLineSegment(sketch, "E398.3.0.0", {"start": v(150, 78.7) * mm, "end": v(150, 76.2) * mm, "construction": true});
            skLineSegment(sketch, "E398.3.1.0", {"start": v(150, 2.5) * mm, "end": v(150, 0) * mm, "construction": true});
            skLineSegment(sketch, "E398.3.2.0", {"start": v(150, -73.7) * mm, "end": v(150, -76.2) * mm, "construction": true});
            skLineSegment(sketch, "E398.direction1", {"start": v(-150, 76.2) * mm, "end": v(-50, 76.2) * mm, "construction": true});
            skLineSegment(sketch, "E398.direction2", {"start": v(-150, 76.2) * mm, "end": v(-150, 0) * mm, "construction": true});
            skSolve(sketch);
        }
        {
            var Q0;
            Q0=sQuery(id+"F10.wireOp",VERTEX,"E396.end");
            var Q1;
            Q1=sQuery(id+"F10.wireOp",VERTEX,"E398.1.0.0.end");
            var Q2;
            Q2=sQuery(id+"F10.wireOp",VERTEX,"E398.2.0.0.end");
            var Q3;
            Q3=sQuery(id+"F10.wireOp",VERTEX,"E398.3.0.0.end");
            var Q4;
            Q4=sQuery(id+"F10.wireOp",VERTEX,"E398.3.1.0.end");
            var Q5;
            Q5=sQuery(id+"F10.wireOp",VERTEX,"E398.1.1.0.end");
            var Q6;
            Q6=sQuery(id+"F10.wireOp",VERTEX,"E398.2.1.0.end");
            var Q7;
            Q7=sQuery(id+"F10.wireOp",VERTEX,"E398.0.2.0.end");
            var Q8;
            Q8=sQuery(id+"F10.wireOp",VERTEX,"E398.3.2.0.end");
            var Q9;
            Q9=sQuery(id+"F10.wireOp",VERTEX,"E398.1.2.0.end");
            var Q10;
            Q10=sQuery(id+"F10.wireOp",VERTEX,"E398.2.2.0.end");
            var Q11;
            Q11=sQuery(id+"F10.wireOp",VERTEX,"E398.0.1.0.end");
            var Q12;
            Q12=makeQuery(id+"F1.opExtrude","SWEPT_BODY",BODY,{"disambiguationData":[OSD([sQuery(id+"F0.wireOp",EDGE,"E0"),sQuery(id+"F0.wireOp",EDGE,"E1"),sQuery(id+"F0.wireOp",EDGE,"E2"),sQuery(id+"F0.wireOp",EDGE,"E3"),sQuery(id+"F0.wireOp",EDGE,"E4"),sQuery(id+"F0.wireOp",EDGE,"E5"),sQuery(id+"F0.wireOp",EDGE,"E6"),sQuery(id+"F0.wireOp",EDGE,"E7"),sQuery(id+"F0.wireOp",EDGE,"E8"),sQuery(id+"F0.wireOp",EDGE,"E9"),sQuery(id+"F0.wireOp",EDGE,"E10"),sQuery(id+"F0.wireOp",EDGE,"E11"),sQuery(id+"F0.wireOp",EDGE,"E12"),sQuery(id+"F0.wireOp",EDGE,"E13"),sQuery(id+"F0.wireOp",EDGE,"E14"),sQuery(id+"F0.wireOp",EDGE,"E15"),sQuery(id+"F0.wireOp",EDGE,"E16"),sQuery(id+"F0.wireOp",EDGE,"E17"),sQuery(id+"F0.wireOp",EDGE,"E18"),sQuery(id+"F0.wireOp",EDGE,"E19"),sQuery(id+"F0.wireOp",EDGE,"E20"),sQuery(id+"F0.wireOp",EDGE,"E21"),sQuery(id+"F0.wireOp",EDGE,"E22"),sQuery(id+"F0.wireOp",EDGE,"E23"),sQuery(id+"F0.wireOp",EDGE,"E24"),sQuery(id+"F0.wireOp",EDGE,"E25"),sQuery(id+"F0.wireOp",EDGE,"E26"),sQuery(id+"F0.wireOp",EDGE,"E27"),sQuery(id+"F0.wireOp",EDGE,"E28"),sQuery(id+"F0.wireOp",EDGE,"E29"),sQuery(id+"F0.wireOp",EDGE,"E30"),sQuery(id+"F0.wireOp",EDGE,"E31"),sQuery(id+"F0.wireOp",EDGE,"E32"),sQuery(id+"F0.wireOp",EDGE,"E33"),sQuery(id+"F0.wireOp",EDGE,"E34"),sQuery(id+"F0.wireOp",EDGE,"E35"),sQuery(id+"F0.wireOp",EDGE,"E36"),sQuery(id+"F0.wireOp",EDGE,"E37"),sQuery(id+"F0.wireOp",EDGE,"E38"),sQuery(id+"F0.wireOp",EDGE,"E39"),sQuery(id+"F0.wireOp",EDGE,"E40"),sQuery(id+"F0.wireOp",EDGE,"E41"),sQuery(id+"F0.wireOp",EDGE,"E42"),sQuery(id+"F0.wireOp",EDGE,"E43"),sQuery(id+"F0.wireOp",EDGE,"E44"),sQuery(id+"F0.wireOp",EDGE,"E45"),sQuery(id+"F0.wireOp",EDGE,"E46"),sQuery(id+"F0.wireOp",EDGE,"E47"),sQuery(id+"F0.wireOp",EDGE,"E48"),sQuery(id+"F0.wireOp",EDGE,"E49"),sQuery(id+"F0.wireOp",EDGE,"E50"),sQuery(id+"F0.wireOp",EDGE,"E51"),sQuery(id+"F0.wireOp",EDGE,"E52"),sQuery(id+"F0.wireOp",EDGE,"E53"),sQuery(id+"F0.wireOp",EDGE,"E54"),sQuery(id+"F0.wireOp",EDGE,"E55"),sQuery(id+"F0.wireOp",EDGE,"E56"),sQuery(id+"F0.wireOp",EDGE,"E57"),sQuery(id+"F0.wireOp",EDGE,"E58"),sQuery(id+"F0.wireOp",EDGE,"E59"),sQuery(id+"F0.wireOp",EDGE,"E60"),sQuery(id+"F0.wireOp",EDGE,"E61"),sQuery(id+"F0.wireOp",EDGE,"E62"),sQuery(id+"F0.wireOp",EDGE,"E63"),sQuery(id+"F0.wireOp",EDGE,"E64"),sQuery(id+"F0.wireOp",EDGE,"E65"),sQuery(id+"F0.wireOp",EDGE,"E66"),sQuery(id+"F0.wireOp",EDGE,"E67"),sQuery(id+"F0.wireOp",EDGE,"E68"),sQuery(id+"F0.wireOp",EDGE,"E69"),sQuery(id+"F0.wireOp",EDGE,"E70"),sQuery(id+"F0.wireOp",EDGE,"E71"),sQuery(id+"F0.wireOp",EDGE,"E72"),sQuery(id+"F0.wireOp",EDGE,"E73"),sQuery(id+"F0.wireOp",EDGE,"E74"),sQuery(id+"F0.wireOp",EDGE,"E75"),sQuery(id+"F0.wireOp",EDGE,"E76"),sQuery(id+"F0.wireOp",EDGE,"E77"),sQuery(id+"F0.wireOp",EDGE,"E78"),sQuery(id+"F0.wireOp",EDGE,"E79"),sQuery(id+"F0.wireOp",EDGE,"E80"),sQuery(id+"F0.wireOp",EDGE,"E81"),sQuery(id+"F0.wireOp",EDGE,"E82"),sQuery(id+"F0.wireOp",EDGE,"E83"),sQuery(id+"F0.wireOp",EDGE,"E84"),sQuery(id+"F0.wireOp",EDGE,"E85"),sQuery(id+"F0.wireOp",EDGE,"E86"),sQuery(id+"F0.wireOp",EDGE,"E87"),sQuery(id+"F0.wireOp",EDGE,"E88"),sQuery(id+"F0.wireOp",EDGE,"E89"),sQuery(id+"F0.wireOp",EDGE,"E90"),sQuery(id+"F0.wireOp",EDGE,"E91"),sQuery(id+"F0.wireOp",EDGE,"E92"),sQuery(id+"F0.wireOp",EDGE,"E93"),sQuery(id+"F0.wireOp",EDGE,"E94"),sQuery(id+"F0.wireOp",EDGE,"E95"),sQuery(id+"F0.wireOp",EDGE,"E96"),sQuery(id+"F0.wireOp",EDGE,"E97"),sQuery(id+"F0.wireOp",EDGE,"E98"),sQuery(id+"F0.wireOp",EDGE,"E99"),sQuery(id+"F0.wireOp",EDGE,"E100"),sQuery(id+"F0.wireOp",EDGE,"E101"),sQuery(id+"F0.wireOp",EDGE,"E102"),sQuery(id+"F0.wireOp",EDGE,"E103"),sQuery(id+"F0.wireOp",EDGE,"E104"),sQuery(id+"F0.wireOp",EDGE,"E105"),sQuery(id+"F0.wireOp",EDGE,"E106"),sQuery(id+"F0.wireOp",EDGE,"E107"),sQuery(id+"F0.wireOp",EDGE,"E108"),sQuery(id+"F0.wireOp",EDGE,"E109"),sQuery(id+"F0.wireOp",EDGE,"E110"),sQuery(id+"F0.wireOp",EDGE,"E111"),sQuery(id+"F0.wireOp",EDGE,"E112"),sQuery(id+"F0.wireOp",EDGE,"E113"),sQuery(id+"F0.wireOp",EDGE,"E114"),sQuery(id+"F0.wireOp",EDGE,"E115"),sQuery(id+"F0.wireOp",EDGE,"E116"),sQuery(id+"F0.wireOp",EDGE,"E117"),sQuery(id+"F0.wireOp",EDGE,"E118"),sQuery(id+"F0.wireOp",EDGE,"E119"),sQuery(id+"F0.wireOp",EDGE,"E120"),sQuery(id+"F0.wireOp",EDGE,"E121"),sQuery(id+"F0.wireOp",EDGE,"E122"),sQuery(id+"F0.wireOp",EDGE,"E123"),sQuery(id+"F0.wireOp",EDGE,"E124"),sQuery(id+"F0.wireOp",EDGE,"E125"),sQuery(id+"F0.wireOp",EDGE,"E126"),sQuery(id+"F0.wireOp",EDGE,"E127"),sQuery(id+"F0.wireOp",EDGE,"E128"),sQuery(id+"F0.wireOp",EDGE,"E129"),sQuery(id+"F0.wireOp",EDGE,"E130"),sQuery(id+"F0.wireOp",EDGE,"E131"),sQuery(id+"F0.wireOp",EDGE,"E132"),sQuery(id+"F0.wireOp",EDGE,"E133"),sQuery(id+"F0.wireOp",EDGE,"E134"),sQuery(id+"F0.wireOp",EDGE,"E135"),sQuery(id+"F0.wireOp",EDGE,"E136"),sQuery(id+"F0.wireOp",EDGE,"E137"),sQuery(id+"F0.wireOp",EDGE,"E138"),sQuery(id+"F0.wireOp",EDGE,"E139"),sQuery(id+"F0.wireOp",EDGE,"E140"),sQuery(id+"F0.wireOp",EDGE,"E141"),sQuery(id+"F0.wireOp",EDGE,"E142"),sQuery(id+"F0.wireOp",EDGE,"E143"),sQuery(id+"F0.wireOp",EDGE,"E144"),sQuery(id+"F0.wireOp",EDGE,"E145"),sQuery(id+"F0.wireOp",EDGE,"E146"),sQuery(id+"F0.wireOp",EDGE,"E147"),sQuery(id+"F0.wireOp",EDGE,"E148"),sQuery(id+"F0.wireOp",EDGE,"E149"),sQuery(id+"F0.wireOp",EDGE,"E150"),sQuery(id+"F0.wireOp",EDGE,"E151"),sQuery(id+"F0.wireOp",EDGE,"E152"),sQuery(id+"F0.wireOp",EDGE,"E153"),sQuery(id+"F0.wireOp",EDGE,"E154"),sQuery(id+"F0.wireOp",EDGE,"E155"),sQuery(id+"F0.wireOp",EDGE,"E156"),sQuery(id+"F0.wireOp",EDGE,"E157"),sQuery(id+"F0.wireOp",EDGE,"E158"),sQuery(id+"F0.wireOp",EDGE,"E159"),sQuery(id+"F0.wireOp",EDGE,"E160"),sQuery(id+"F0.wireOp",EDGE,"E161"),sQuery(id+"F0.wireOp",EDGE,"E162"),sQuery(id+"F0.wireOp",EDGE,"E163"),sQuery(id+"F0.wireOp",EDGE,"E164"),sQuery(id+"F0.wireOp",EDGE,"E165"),sQuery(id+"F0.wireOp",EDGE,"E166"),sQuery(id+"F0.wireOp",EDGE,"E167"),sQuery(id+"F0.wireOp",EDGE,"E168"),sQuery(id+"F0.wireOp",EDGE,"E169"),sQuery(id+"F0.wireOp",EDGE,"E170"),sQuery(id+"F0.wireOp",EDGE,"E171"),sQuery(id+"F0.wireOp",EDGE,"E172"),sQuery(id+"F0.wireOp",EDGE,"E173"),sQuery(id+"F0.wireOp",EDGE,"E174"),sQuery(id+"F0.wireOp",EDGE,"E175"),sQuery(id+"F0.wireOp",EDGE,"E176"),sQuery(id+"F0.wireOp",EDGE,"E177"),sQuery(id+"F0.wireOp",EDGE,"E178"),sQuery(id+"F0.wireOp",EDGE,"E179"),sQuery(id+"F0.wireOp",EDGE,"E180"),sQuery(id+"F0.wireOp",EDGE,"E181"),sQuery(id+"F0.wireOp",EDGE,"E182"),sQuery(id+"F0.wireOp",EDGE,"E183"),sQuery(id+"F0.wireOp",EDGE,"E184"),sQuery(id+"F0.wireOp",EDGE,"E185"),sQuery(id+"F0.wireOp",EDGE,"E186"),sQuery(id+"F0.wireOp",EDGE,"E187"),sQuery(id+"F0.wireOp",EDGE,"E188"),sQuery(id+"F0.wireOp",EDGE,"E189"),sQuery(id+"F0.wireOp",EDGE,"E190"),sQuery(id+"F0.wireOp",EDGE,"E191"),sQuery(id+"F0.wireOp",EDGE,"E192"),sQuery(id+"F0.wireOp",EDGE,"E193"),sQuery(id+"F0.wireOp",EDGE,"E194"),sQuery(id+"F0.wireOp",EDGE,"E195"),sQuery(id+"F0.wireOp",EDGE,"E196"),sQuery(id+"F0.wireOp",EDGE,"E197"),sQuery(id+"F0.wireOp",EDGE,"E198"),sQuery(id+"F0.wireOp",EDGE,"E199"),sQuery(id+"F0.wireOp",EDGE,"E200"),sQuery(id+"F0.wireOp",EDGE,"E201"),sQuery(id+"F0.wireOp",EDGE,"E202"),sQuery(id+"F0.wireOp",EDGE,"E203"),sQuery(id+"F0.wireOp",EDGE,"E204"),sQuery(id+"F0.wireOp",EDGE,"E205"),sQuery(id+"F0.wireOp",EDGE,"E206"),sQuery(id+"F0.wireOp",EDGE,"E207"),sQuery(id+"F0.wireOp",EDGE,"E208"),sQuery(id+"F0.wireOp",EDGE,"E209"),sQuery(id+"F0.wireOp",EDGE,"E210"),sQuery(id+"F0.wireOp",EDGE,"E211"),sQuery(id+"F0.wireOp",EDGE,"E212"),sQuery(id+"F0.wireOp",EDGE,"E213"),sQuery(id+"F0.wireOp",EDGE,"E214"),sQuery(id+"F0.wireOp",EDGE,"E215"),sQuery(id+"F0.wireOp",EDGE,"E216"),sQuery(id+"F0.wireOp",EDGE,"E217"),sQuery(id+"F0.wireOp",EDGE,"E218"),sQuery(id+"F0.wireOp",EDGE,"E219"),sQuery(id+"F0.wireOp",EDGE,"E220"),sQuery(id+"F0.wireOp",EDGE,"E221"),sQuery(id+"F0.wireOp",EDGE,"E222"),sQuery(id+"F0.wireOp",EDGE,"E223"),sQuery(id+"F0.wireOp",EDGE,"E224"),sQuery(id+"F0.wireOp",EDGE,"E225"),sQuery(id+"F0.wireOp",EDGE,"E226"),sQuery(id+"F0.wireOp",EDGE,"E227"),sQuery(id+"F0.wireOp",EDGE,"E228"),sQuery(id+"F0.wireOp",EDGE,"E229"),sQuery(id+"F0.wireOp",EDGE,"E230"),sQuery(id+"F0.wireOp",EDGE,"E231"),sQuery(id+"F0.wireOp",EDGE,"E232"),sQuery(id+"F0.wireOp",EDGE,"E233"),sQuery(id+"F0.wireOp",EDGE,"E234"),sQuery(id+"F0.wireOp",EDGE,"E235"),sQuery(id+"F0.wireOp",EDGE,"E236"),sQuery(id+"F0.wireOp",EDGE,"E237"),sQuery(id+"F0.wireOp",EDGE,"E238"),sQuery(id+"F0.wireOp",EDGE,"E239"),sQuery(id+"F0.wireOp",EDGE,"E240"),sQuery(id+"F0.wireOp",EDGE,"E241"),sQuery(id+"F0.wireOp",EDGE,"E242"),sQuery(id+"F0.wireOp",EDGE,"E243"),sQuery(id+"F0.wireOp",EDGE,"E244"),sQuery(id+"F0.wireOp",EDGE,"E245"),sQuery(id+"F0.wireOp",EDGE,"E246"),sQuery(id+"F0.wireOp",EDGE,"E247"),sQuery(id+"F0.wireOp",EDGE,"E248"),sQuery(id+"F0.wireOp",EDGE,"E249"),sQuery(id+"F0.wireOp",EDGE,"E250"),sQuery(id+"F0.wireOp",EDGE,"E251"),sQuery(id+"F0.wireOp",EDGE,"E252"),sQuery(id+"F0.wireOp",EDGE,"E253"),sQuery(id+"F0.wireOp",EDGE,"E254"),sQuery(id+"F0.wireOp",EDGE,"E255"),sQuery(id+"F0.wireOp",EDGE,"E256"),sQuery(id+"F0.wireOp",EDGE,"E257"),sQuery(id+"F0.wireOp",EDGE,"E258"),sQuery(id+"F0.wireOp",EDGE,"E259"),sQuery(id+"F0.wireOp",EDGE,"E260"),sQuery(id+"F0.wireOp",EDGE,"E261"),sQuery(id+"F0.wireOp",EDGE,"E262"),sQuery(id+"F0.wireOp",EDGE,"E263"),sQuery(id+"F0.wireOp",EDGE,"E264"),sQuery(id+"F0.wireOp",EDGE,"E265"),sQuery(id+"F0.wireOp",EDGE,"E266"),sQuery(id+"F0.wireOp",EDGE,"E267"),sQuery(id+"F0.wireOp",EDGE,"E268"),sQuery(id+"F0.wireOp",EDGE,"E269"),sQuery(id+"F0.wireOp",EDGE,"E270"),sQuery(id+"F0.wireOp",EDGE,"E271"),sQuery(id+"F0.wireOp",EDGE,"E272"),sQuery(id+"F0.wireOp",EDGE,"E273"),sQuery(id+"F0.wireOp",EDGE,"E274"),sQuery(id+"F0.wireOp",EDGE,"E275"),sQuery(id+"F0.wireOp",EDGE,"E276"),sQuery(id+"F0.wireOp",EDGE,"E277"),sQuery(id+"F0.wireOp",EDGE,"E278"),sQuery(id+"F0.wireOp",EDGE,"E279"),sQuery(id+"F0.wireOp",EDGE,"E280"),sQuery(id+"F0.wireOp",EDGE,"E281"),sQuery(id+"F0.wireOp",EDGE,"E282"),sQuery(id+"F0.wireOp",EDGE,"E283"),sQuery(id+"F0.wireOp",EDGE,"E284"),sQuery(id+"F0.wireOp",EDGE,"E285"),sQuery(id+"F0.wireOp",EDGE,"E286"),sQuery(id+"F0.wireOp",EDGE,"E287"),sQuery(id+"F0.wireOp",EDGE,"E288"),sQuery(id+"F0.wireOp",EDGE,"E289"),sQuery(id+"F0.wireOp",EDGE,"E290"),sQuery(id+"F0.wireOp",EDGE,"E291")])]});
            hole(context, id + "F11", {"style" : HoleStyle.SIMPLE, "endStyle" : HoleEndStyle.THROUGH, "standardTappedOrClearance" : lookupTablePath({ "standard" : "ISO", "size" : "3.4", "type" : "Drilled" }), "standardBlindInLast" : lookupTablePath({ "standard" : "ISO", "size" : "3.4", "type" : "Drilled" }), "holeDiameter" : 3.4 * mm, "majorDiameter" : 5 * mm, "isTappedThrough" : true, "tappedDepth" : 12 * mm, "tapClearance" : 3, "locations" : qUnion([Q0, Q1, Q2, Q3, Q4, Q5, Q6, Q7, Q8, Q9, Q10, Q11]), "scope" : qUnion([Q12])});
        }
    });
